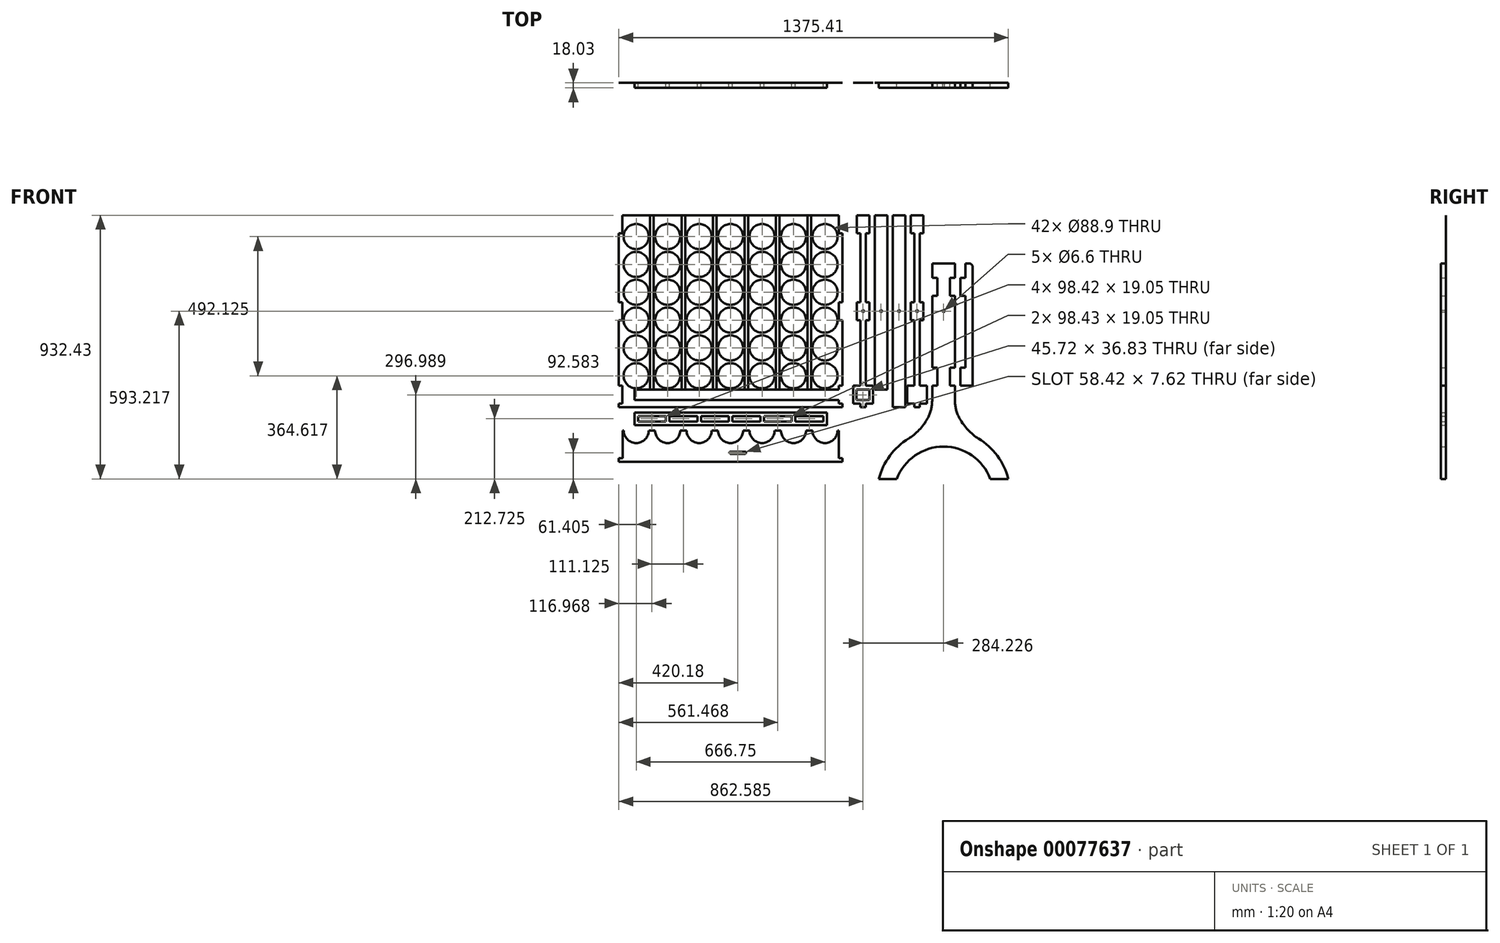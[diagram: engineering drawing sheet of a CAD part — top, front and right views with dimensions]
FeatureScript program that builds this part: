
annotation { "Feature Type Name" : "Feature", "Feature Type Description" : "" }
export const myFeature = defineFeature(function(context is Context, id is Id, definition is map)
    precondition{}
    {
        {
            assignVariable(context, id + "F0", {"name" : "Thickness", "anyValue" : .48});
        }
        {
            var Q0;
            Q0=qCreatedBy(makeId("Front.planeOp"),FACE);
            var sketch = newSketch(context, id + "F1", { "sketchPlane" : qUnion([Q0])});
            skLineSegment(sketch, "E0.bottom", {"start": v(-1056.26, 310.13) * mm, "end": v(-266.7, 310.13) * mm});
            skLineSegment(sketch, "E0.top", {"start": v(-1056.26, -368.3) * mm, "end": v(-266.7, -368.3) * mm});
            skLineSegment(sketch, "E0.left", {"start": v(-1056.26, 310.13) * mm, "end": v(-1056.26, -368.3) * mm});
            skLineSegment(sketch, "E0.right", {"start": v(-266.7, 310.13) * mm, "end": v(-266.7, -368.3) * mm});
            skCircle(sketch, "E1", {"center": v(-994.85, 234.44) * mm, "radius": 44.45 * mm});
            skLineSegment(sketch, "E2.bottom", {"start": v(-1056.26, 310.13) * mm, "end": v(-1044.07, 310.13) * mm});
            skLineSegment(sketch, "E2.right", {"start": v(-1044.07, 310.13) * mm, "end": v(-1044.07, -368.3) * mm, "construction": true});
            skLineSegment(sketch, "E3.0", {"start": v(-278.9, 310.13) * mm, "end": v(-278.9, -368.3) * mm, "construction": true});
            skLineSegment(sketch, "E4.top", {"start": v(-1056.26, 246.63) * mm, "end": v(-1044.07, 246.63) * mm});
            skLineSegment(sketch, "E4.left", {"start": v(-1056.26, 310.13) * mm, "end": v(-1056.26, 246.63) * mm});
            skLineSegment(sketch, "E4.right", {"start": v(-1044.07, 310.13) * mm, "end": v(-1044.07, 246.63) * mm});
            skLineSegment(sketch, "E5.bottom", {"start": v(-266.7, 310.13) * mm, "end": v(-278.9, 310.13) * mm});
            skLineSegment(sketch, "E5.top", {"start": v(-266.7, 246.63) * mm, "end": v(-278.9, 246.63) * mm});
            skLineSegment(sketch, "E5.left", {"start": v(-266.7, 310.13) * mm, "end": v(-266.7, 246.63) * mm});
            skLineSegment(sketch, "E5.right", {"start": v(-278.9, 310.13) * mm, "end": v(-278.9, 246.63) * mm});
            skLineSegment(sketch, "E6.top", {"start": v(-266.7, -292.1) * mm, "end": v(-278.9, -292.1) * mm});
            skLineSegment(sketch, "E6.left", {"start": v(-266.7, -368.3) * mm, "end": v(-266.7, -292.1) * mm});
            skLineSegment(sketch, "E6.right", {"start": v(-278.9, -355.6) * mm, "end": v(-278.9, -292.1) * mm});
            skLineSegment(sketch, "E7.bottom", {"start": v(-1056.26, 2.67) * mm, "end": v(-1044.07, 2.67) * mm});
            skLineSegment(sketch, "E7.top", {"start": v(-1056.26, -60.83) * mm, "end": v(-1044.07, -60.83) * mm});
            skLineSegment(sketch, "E7.left", {"start": v(-1056.26, 2.67) * mm, "end": v(-1056.26, -60.83) * mm});
            skLineSegment(sketch, "E7.right", {"start": v(-1044.07, 2.67) * mm, "end": v(-1044.07, -60.83) * mm});
            skPoint(sketch, "E8", {"position": v(-1056.26, -29.08) * mm});
            skLineSegment(sketch, "E9.MirrorCS", {"start": v(-266.7, -60.83) * mm, "end": v(-278.9, -60.83) * mm});
            skLineSegment(sketch, "E10.MirrorCS", {"start": v(-266.7, 2.67) * mm, "end": v(-278.9, 2.67) * mm});
            skLineSegment(sketch, "E11.MirrorCS", {"start": v(-266.7, 2.67) * mm, "end": v(-266.7, -60.83) * mm});
            skLineSegment(sketch, "E12.MirrorCS", {"start": v(-278.9, 2.67) * mm, "end": v(-278.9, -60.83) * mm});
            skLineSegment(sketch, "E13", {"start": v(-1044.07, -306.9) * mm, "end": v(-278.9, -306.9) * mm});
            skLineSegment(sketch, "E14", {"start": v(-945.64, 310.13) * mm, "end": v(-945.64, -306.9) * mm});
            skLineSegment(sketch, "E15", {"start": v(-932.94, 310.13) * mm, "end": v(-932.94, -306.9) * mm});
            skLineSegment(sketch, "E16.1.0.0", {"start": v(-821.82, 310.13) * mm, "end": v(-821.82, -306.9) * mm});
            skLineSegment(sketch, "E16.1.0.1", {"start": v(-834.52, 310.13) * mm, "end": v(-834.52, -306.9) * mm});
            skLineSegment(sketch, "E16.2.0.0", {"start": v(-710.7, 310.13) * mm, "end": v(-710.7, -306.9) * mm});
            skLineSegment(sketch, "E16.2.0.1", {"start": v(-723.4, 310.13) * mm, "end": v(-723.4, -306.9) * mm});
            skLineSegment(sketch, "E16.3.0.0", {"start": v(-599.57, 310.13) * mm, "end": v(-599.57, -306.9) * mm});
            skLineSegment(sketch, "E16.3.0.1", {"start": v(-612.27, 310.13) * mm, "end": v(-612.27, -306.9) * mm});
            skLineSegment(sketch, "E16.4.0.0", {"start": v(-488.44, 310.13) * mm, "end": v(-488.44, -306.9) * mm});
            skLineSegment(sketch, "E16.4.0.1", {"start": v(-501.14, 310.13) * mm, "end": v(-501.14, -306.9) * mm});
            skLineSegment(sketch, "E16.5.0.0", {"start": v(-377.32, 310.13) * mm, "end": v(-377.32, -306.9) * mm});
            skLineSegment(sketch, "E16.5.0.1", {"start": v(-390.02, 310.13) * mm, "end": v(-390.02, -306.9) * mm});
            skLineSegment(sketch, "E16.direction1", {"start": v(-932.94, -306.9) * mm, "end": v(-821.82, -306.9) * mm, "construction": true});
            skLineSegment(sketch, "E17.bottom", {"start": v(-994.85, -387.35) * mm, "end": v(-328.1, -387.35) * mm});
            skLineSegment(sketch, "E17.top", {"start": v(-994.85, -431.8) * mm, "end": v(-328.1, -431.8) * mm});
            skLineSegment(sketch, "E17.left", {"start": v(-994.85, -387.35) * mm, "end": v(-994.85, -431.8) * mm, "construction": true});
            skLineSegment(sketch, "E17.right", {"start": v(-328.1, -387.35) * mm, "end": v(-328.1, -431.8) * mm, "construction": true});
            skLineSegment(sketch, "E18.bottom", {"start": v(-988.5, -387.35) * mm, "end": v(-1001.2, -387.35) * mm});
            skLineSegment(sketch, "E18.top", {"start": v(-988.5, -431.8) * mm, "end": v(-1001.2, -431.8) * mm});
            skLineSegment(sketch, "E18.left", {"start": v(-988.5, -387.35) * mm, "end": v(-988.5, -431.8) * mm});
            skLineSegment(sketch, "E18.right", {"start": v(-1001.2, -387.35) * mm, "end": v(-1001.2, -431.8) * mm});
            skPoint(sketch, "E18.middle", {"position": v(-994.85, -409.58) * mm});
            skLineSegment(sketch, "E19.1.0.0", {"start": v(-877.38, -387.35) * mm, "end": v(-877.38, -431.8) * mm});
            skLineSegment(sketch, "E19.1.0.1", {"start": v(-890.08, -387.35) * mm, "end": v(-890.08, -431.8) * mm});
            skLineSegment(sketch, "E19.2.0.0", {"start": v(-766.25, -387.35) * mm, "end": v(-766.25, -431.8) * mm});
            skLineSegment(sketch, "E19.2.0.1", {"start": v(-778.95, -387.35) * mm, "end": v(-778.95, -431.8) * mm});
            skLineSegment(sketch, "E19.3.0.0", {"start": v(-655.13, -387.35) * mm, "end": v(-655.13, -431.8) * mm});
            skLineSegment(sketch, "E19.3.0.1", {"start": v(-667.83, -387.35) * mm, "end": v(-667.83, -431.8) * mm});
            skLineSegment(sketch, "E19.4.0.0", {"start": v(-544, -387.35) * mm, "end": v(-544, -431.8) * mm});
            skLineSegment(sketch, "E19.4.0.1", {"start": v(-556.7, -387.35) * mm, "end": v(-556.7, -431.8) * mm});
            skLineSegment(sketch, "E19.5.0.0", {"start": v(-432.88, -387.35) * mm, "end": v(-432.88, -431.8) * mm});
            skLineSegment(sketch, "E19.5.0.1", {"start": v(-445.58, -387.35) * mm, "end": v(-445.58, -431.8) * mm});
            skLineSegment(sketch, "E19.6.0.0", {"start": v(-321.75, -387.35) * mm, "end": v(-321.75, -431.8) * mm});
            skLineSegment(sketch, "E19.6.0.1", {"start": v(-334.45, -387.35) * mm, "end": v(-334.45, -431.8) * mm});
            skLineSegment(sketch, "E19.direction1", {"start": v(-988.5, -431.8) * mm, "end": v(-877.38, -431.8) * mm, "construction": true});
            skLineSegment(sketch, "E20", {"start": v(-321.75, -387.35) * mm, "end": v(-328.1, -387.35) * mm});
            skLineSegment(sketch, "E21", {"start": v(-321.75, -431.8) * mm, "end": v(-328.1, -431.8) * mm});
            skLineSegment(sketch, "E22", {"start": v(-988.5, -409.58) * mm, "end": v(-890.08, -409.58) * mm, "construction": true});
            skLineSegment(sketch, "E23.0", {"start": v(-988.5, -419.1) * mm, "end": v(-890.08, -419.1) * mm});
            skLineSegment(sketch, "E24.0", {"start": v(-988.5, -400.05) * mm, "end": v(-890.08, -400.05) * mm});
            skLineSegment(sketch, "E25.1.0.0", {"start": v(-877.38, -400.05) * mm, "end": v(-778.95, -400.05) * mm});
            skLineSegment(sketch, "E25.1.0.1", {"start": v(-877.38, -419.1) * mm, "end": v(-778.95, -419.1) * mm});
            skLineSegment(sketch, "E25.2.0.0", {"start": v(-766.25, -400.05) * mm, "end": v(-667.83, -400.05) * mm});
            skLineSegment(sketch, "E25.2.0.1", {"start": v(-766.25, -419.1) * mm, "end": v(-667.83, -419.1) * mm});
            skLineSegment(sketch, "E25.3.0.0", {"start": v(-655.13, -400.05) * mm, "end": v(-556.7, -400.05) * mm});
            skLineSegment(sketch, "E25.3.0.1", {"start": v(-655.13, -419.1) * mm, "end": v(-556.7, -419.1) * mm});
            skLineSegment(sketch, "E25.4.0.0", {"start": v(-544, -400.05) * mm, "end": v(-445.58, -400.05) * mm});
            skLineSegment(sketch, "E25.4.0.1", {"start": v(-544, -419.1) * mm, "end": v(-445.58, -419.1) * mm});
            skLineSegment(sketch, "E25.5.0.0", {"start": v(-432.88, -400.05) * mm, "end": v(-334.45, -400.05) * mm});
            skLineSegment(sketch, "E25.5.0.1", {"start": v(-432.88, -419.1) * mm, "end": v(-334.45, -419.1) * mm});
            skLineSegment(sketch, "E25.direction1", {"start": v(-988.5, -400.05) * mm, "end": v(-877.38, -400.05) * mm, "construction": true});
            skLineSegment(sketch, "E26.0", {"start": v(-1044.07, -343.73) * mm, "end": v(-278.9, -343.73) * mm});
            skLineSegment(sketch, "E27", {"start": v(-278.9, -355.6) * mm, "end": v(-266.7, -355.6) * mm});
            skLineSegment(sketch, "E28", {"start": v(-661.48, -368.3) * mm, "end": v(-661.48, -343.73) * mm, "construction": true});
            skLineSegment(sketch, "E29.MirrorCS", {"start": v(-1044.07, -355.6) * mm, "end": v(-1056.26, -355.6) * mm});
            skLineSegment(sketch, "E30.MirrorCS", {"start": v(-1044.07, -355.6) * mm, "end": v(-1044.07, -292.1) * mm});
            skLineSegment(sketch, "E31.MirrorCS", {"start": v(-1056.26, -292.1) * mm, "end": v(-1044.07, -292.1) * mm});
            skLineSegment(sketch, "E32", {"start": v(-1001.2, -343.73) * mm, "end": v(-1001.2, -306.9) * mm});
            skLineSegment(sketch, "E33.bottom", {"start": v(-215.9, 310.13) * mm, "end": v(-171.45, 310.13) * mm, "construction": true});
            skLineSegment(sketch, "E34.bottom", {"start": v(-228.1, -355.6) * mm, "end": v(-203.7, -355.6) * mm});
            skLineSegment(sketch, "E34.top", {"start": v(-228.1, -292.1) * mm, "end": v(-203.7, -292.1) * mm});
            skLineSegment(sketch, "E34.left", {"start": v(-228.1, -355.6) * mm, "end": v(-228.1, -292.1) * mm});
            skLineSegment(sketch, "E34.right", {"start": v(-203.7, -355.6) * mm, "end": v(-203.7, -292.1) * mm});
            skLineSegment(sketch, "E35", {"start": v(-193.67, -368.3) * mm, "end": v(-193.67, 310.13) * mm, "construction": true});
            skLineSegment(sketch, "E36.bottom", {"start": v(-215.9, 2.67) * mm, "end": v(-203.7, 2.67) * mm});
            skLineSegment(sketch, "E36.top", {"start": v(-215.9, -60.83) * mm, "end": v(-203.7, -60.83) * mm});
            skLineSegment(sketch, "E36.left", {"start": v(-215.9, 2.67) * mm, "end": v(-215.9, -60.83) * mm});
            skLineSegment(sketch, "E36.right", {"start": v(-203.7, 2.67) * mm, "end": v(-203.7, -60.83) * mm});
            skLineSegment(sketch, "E37.bottom", {"start": v(-215.9, 310.13) * mm, "end": v(-203.7, 310.13) * mm});
            skLineSegment(sketch, "E37.top", {"start": v(-215.9, 246.63) * mm, "end": v(-203.7, 246.63) * mm});
            skLineSegment(sketch, "E37.left", {"start": v(-215.9, 310.13) * mm, "end": v(-215.9, 246.63) * mm});
            skLineSegment(sketch, "E37.right", {"start": v(-203.7, 310.13) * mm, "end": v(-203.7, 246.63) * mm});
            skLineSegment(sketch, "E38.MirrorCS", {"start": v(-171.45, 310.13) * mm, "end": v(-171.45, 246.63) * mm});
            skLineSegment(sketch, "E39.MirrorCS", {"start": v(-171.45, 310.13) * mm, "end": v(-183.64, 310.13) * mm});
            skLineSegment(sketch, "E40.MirrorCS", {"start": v(-183.64, 310.13) * mm, "end": v(-183.64, 246.63) * mm});
            skLineSegment(sketch, "E41.MirrorCS", {"start": v(-171.45, 246.63) * mm, "end": v(-183.64, 246.63) * mm});
            skLineSegment(sketch, "E42.MirrorCS", {"start": v(-171.45, 2.67) * mm, "end": v(-171.45, -60.83) * mm});
            skLineSegment(sketch, "E43.MirrorCS", {"start": v(-171.45, -60.83) * mm, "end": v(-183.64, -60.83) * mm});
            skLineSegment(sketch, "E44.MirrorCS", {"start": v(-183.64, 2.67) * mm, "end": v(-183.64, -60.83) * mm});
            skLineSegment(sketch, "E45.MirrorCS", {"start": v(-171.45, 2.67) * mm, "end": v(-183.64, 2.67) * mm});
            skLineSegment(sketch, "E46.MirrorCS", {"start": v(-159.26, -355.6) * mm, "end": v(-159.26, -292.1) * mm});
            skLineSegment(sketch, "E47.MirrorCS", {"start": v(-159.26, -355.6) * mm, "end": v(-183.64, -355.6) * mm});
            skLineSegment(sketch, "E48.MirrorCS", {"start": v(-159.26, -292.1) * mm, "end": v(-183.64, -292.1) * mm});
            skLineSegment(sketch, "E49.MirrorCS", {"start": v(-183.64, -355.6) * mm, "end": v(-183.64, -292.1) * mm});
            skLineSegment(sketch, "E50.bottom", {"start": v(-203.7, -368.3) * mm, "end": v(-183.64, -368.3) * mm});
            skLineSegment(sketch, "E50.top", {"start": v(-203.7, 310.13) * mm, "end": v(-183.64, 310.13) * mm});
            skLineSegment(sketch, "E50.left", {"start": v(-203.7, -368.3) * mm, "end": v(-203.7, 310.13) * mm});
            skLineSegment(sketch, "E50.right", {"start": v(-183.64, -368.3) * mm, "end": v(-183.64, 310.13) * mm});
            skLineSegment(sketch, "E51.bottom", {"start": v(-216.54, -306.9) * mm, "end": v(-170.82, -306.9) * mm});
            skLineSegment(sketch, "E51.top", {"start": v(-216.54, -343.73) * mm, "end": v(-170.82, -343.73) * mm});
            skLineSegment(sketch, "E51.left", {"start": v(-216.54, -306.9) * mm, "end": v(-216.54, -343.73) * mm});
            skLineSegment(sketch, "E51.right", {"start": v(-170.82, -306.9) * mm, "end": v(-170.82, -343.73) * mm});
            skPoint(sketch, "E52", {"position": v(-193.68, -306.9) * mm});
            skLineSegment(sketch, "E53.bottom", {"start": v(-152.4, 310.13) * mm, "end": v(-107.95, 310.13) * mm});
            skLineSegment(sketch, "E53.top", {"start": v(-152.4, -368.3) * mm, "end": v(-107.95, -368.3) * mm, "construction": true});
            skLineSegment(sketch, "E53.left", {"start": v(-152.4, 310.13) * mm, "end": v(-152.4, -368.3) * mm});
            skLineSegment(sketch, "E53.right", {"start": v(-107.95, 310.13) * mm, "end": v(-107.95, -368.3) * mm});
            skLineSegment(sketch, "E54.0", {"start": v(-98.43, 532.38) * mm, "end": v(-98.43, -368.3) * mm, "construction": true});
            skLineSegment(sketch, "E55.MirrorCS", {"start": v(19.05, 310.13) * mm, "end": v(6.86, 310.13) * mm});
            skLineSegment(sketch, "E56.MirrorCS", {"start": v(-25.4, 310.13) * mm, "end": v(-13.2, 310.13) * mm});
            skLineSegment(sketch, "E57.MirrorCS", {"start": v(-37.6, -355.6) * mm, "end": v(-13.2, -355.6) * mm});
            skLineSegment(sketch, "E58.MirrorCS", {"start": v(31.24, -355.6) * mm, "end": v(6.86, -355.6) * mm});
            skLineSegment(sketch, "E59.MirrorCS", {"start": v(19.05, -60.83) * mm, "end": v(6.86, -60.83) * mm});
            skLineSegment(sketch, "E60.MirrorCS", {"start": v(19.05, 246.63) * mm, "end": v(6.86, 246.63) * mm});
            skLineSegment(sketch, "E61.MirrorCS", {"start": v(19.05, 310.13) * mm, "end": v(-25.4, 310.13) * mm, "construction": true});
            skLineSegment(sketch, "E62.MirrorCS", {"start": v(-37.6, -292.1) * mm, "end": v(-13.2, -292.1) * mm});
            skLineSegment(sketch, "E63.MirrorCS", {"start": v(-25.4, 246.63) * mm, "end": v(-13.2, 246.63) * mm});
            skLineSegment(sketch, "E64.MirrorCS", {"start": v(31.24, -292.1) * mm, "end": v(6.86, -292.1) * mm});
            skLineSegment(sketch, "E65.MirrorCS", {"start": v(-25.4, -60.83) * mm, "end": v(-13.2, -60.83) * mm});
            skLineSegment(sketch, "E66.MirrorCS", {"start": v(19.05, 2.67) * mm, "end": v(6.86, 2.67) * mm});
            skLineSegment(sketch, "E67.MirrorCS", {"start": v(-25.4, 2.67) * mm, "end": v(-13.2, 2.67) * mm});
            skLineSegment(sketch, "E68.MirrorCS", {"start": v(6.86, 310.13) * mm, "end": v(-13.2, 310.13) * mm});
            skLineSegment(sketch, "E69.MirrorCS", {"start": v(6.86, 2.67) * mm, "end": v(6.86, -60.83) * mm});
            skLineSegment(sketch, "E70.MirrorCS", {"start": v(-13.2, -355.6) * mm, "end": v(-13.2, -292.1) * mm});
            skLineSegment(sketch, "E71.MirrorCS", {"start": v(6.86, -368.3) * mm, "end": v(-13.2, -368.3) * mm});
            skLineSegment(sketch, "E72.MirrorCS", {"start": v(-44.45, -368.3) * mm, "end": v(-88.9, -368.3) * mm});
            skLineSegment(sketch, "E73.MirrorCS", {"start": v(-25.4, 2.67) * mm, "end": v(-25.4, -60.83) * mm});
            skLineSegment(sketch, "E74.MirrorCS", {"start": v(-13.2, 2.67) * mm, "end": v(-13.2, -60.83) * mm});
            skLineSegment(sketch, "E75.MirrorCS", {"start": v(6.86, -355.6) * mm, "end": v(6.86, -292.1) * mm});
            skLineSegment(sketch, "E76.MirrorCS", {"start": v(-37.6, -355.6) * mm, "end": v(-37.6, -292.1) * mm});
            skLineSegment(sketch, "E77.MirrorCS", {"start": v(19.05, 2.67) * mm, "end": v(19.05, -60.83) * mm});
            skLineSegment(sketch, "E78.MirrorCS", {"start": v(-13.2, -368.3) * mm, "end": v(-13.2, 310.13) * mm});
            skLineSegment(sketch, "E79.MirrorCS", {"start": v(-13.2, 310.13) * mm, "end": v(-13.2, 246.63) * mm});
            skPoint(sketch, "E80.MirrorP", {"position": v(-3.18, -306.9) * mm});
            skLineSegment(sketch, "E81.MirrorCS", {"start": v(-25.4, 310.13) * mm, "end": v(-25.4, 246.63) * mm});
            skLineSegment(sketch, "E82.MirrorCS", {"start": v(6.86, 310.13) * mm, "end": v(6.86, 246.63) * mm});
            skLineSegment(sketch, "E83.MirrorCS", {"start": v(19.05, 310.13) * mm, "end": v(19.05, 246.63) * mm});
            skLineSegment(sketch, "E84.MirrorCS", {"start": v(6.86, -368.3) * mm, "end": v(6.86, 310.13) * mm});
            skLineSegment(sketch, "E85.MirrorCS", {"start": v(31.24, -355.6) * mm, "end": v(31.24, -292.1) * mm});
            skLineSegment(sketch, "E86.MirrorCS", {"start": v(-44.45, 310.13) * mm, "end": v(-88.9, 310.13) * mm});
            skLineSegment(sketch, "E87.MirrorCS", {"start": v(-44.45, 310.13) * mm, "end": v(-44.45, -368.3) * mm});
            skLineSegment(sketch, "E88.MirrorCS", {"start": v(-88.9, 310.13) * mm, "end": v(-88.9, -368.3) * mm});
            skLineSegment(sketch, "E89.MirrorCS", {"start": v(-3.18, -368.3) * mm, "end": v(-3.18, 310.13) * mm, "construction": true});
            skLineSegment(sketch, "E90.bottom", {"start": v(-152.4, -306.9) * mm, "end": v(-107.95, -306.9) * mm});
            skLineSegment(sketch, "E90.top", {"start": v(-152.4, -343.73) * mm, "end": v(-107.95, -343.73) * mm, "construction": true});
            skLineSegment(sketch, "E90.left", {"start": v(-152.4, -306.9) * mm, "end": v(-152.4, -343.73) * mm});
            skLineSegment(sketch, "E90.right", {"start": v(-107.95, -306.9) * mm, "end": v(-107.95, -343.73) * mm});
            skLineSegment(sketch, "E91.bottom", {"start": v(-1056.26, -450.85) * mm, "end": v(-266.7, -450.85) * mm});
            skLineSegment(sketch, "E91.top", {"start": v(-1056.26, -561.47) * mm, "end": v(-266.7, -561.47) * mm});
            skLineSegment(sketch, "E91.left", {"start": v(-1056.26, -450.85) * mm, "end": v(-1056.26, -561.47) * mm});
            skLineSegment(sketch, "E91.right", {"start": v(-266.7, -450.85) * mm, "end": v(-266.7, -561.47) * mm});
            skLineSegment(sketch, "E92.bottom", {"start": v(50.3, -368.3) * mm, "end": v(130.8, -368.3) * mm, "construction": true});
            skLineSegment(sketch, "E92.top", {"start": v(50.3, 139.7) * mm, "end": v(130.8, 139.7) * mm});
            skLineSegment(sketch, "E92.left", {"start": v(50.3, -368.3) * mm, "end": v(50.3, 139.7) * mm});
            skLineSegment(sketch, "E92.right", {"start": v(130.8, -368.3) * mm, "end": v(130.8, 139.7) * mm});
            skLineSegment(sketch, "E93", {"start": v(50.3, -368.3) * mm, "end": v(-31.4, -478.48) * mm});
            skLineSegment(sketch, "E94", {"start": v(-138.05, -622.3) * mm, "end": v(319.15, -622.3) * mm});
            skLineSegment(sketch, "E95", {"start": v(319.15, -622.3) * mm, "end": v(212.5, -478.48) * mm, "construction": true});
            skLineSegment(sketch, "E96", {"start": v(90.55, -368.3) * mm, "end": v(90.55, -622.3) * mm, "construction": true});
            skLineSegment(sketch, "E97.bottom", {"start": v(50.3, -292.1) * mm, "end": v(68.33, -292.1) * mm});
            skLineSegment(sketch, "E97.top", {"start": v(50.3, -228.6) * mm, "end": v(68.33, -228.6) * mm});
            skLineSegment(sketch, "E97.left", {"start": v(50.3, -292.1) * mm, "end": v(50.3, -228.6) * mm});
            skLineSegment(sketch, "E97.right", {"start": v(68.33, -292.1) * mm, "end": v(68.33, -228.6) * mm});
            skLineSegment(sketch, "E98.bottom", {"start": v(50.3, 88.9) * mm, "end": v(68.33, 88.9) * mm});
            skLineSegment(sketch, "E98.top", {"start": v(50.3, 25.4) * mm, "end": v(68.33, 25.4) * mm});
            skLineSegment(sketch, "E98.left", {"start": v(50.3, 88.9) * mm, "end": v(50.3, 25.4) * mm});
            skLineSegment(sketch, "E98.right", {"start": v(68.33, 88.9) * mm, "end": v(68.33, 25.4) * mm});
            skLineSegment(sketch, "E99.MirrorCS", {"start": v(130.8, -292.1) * mm, "end": v(112.78, -292.1) * mm});
            skLineSegment(sketch, "E100.MirrorCS", {"start": v(130.81, -228.6) * mm, "end": v(112.78, -228.6) * mm});
            skLineSegment(sketch, "E101.MirrorCS", {"start": v(130.81, -292.1) * mm, "end": v(130.81, -228.6) * mm});
            skLineSegment(sketch, "E102.MirrorCS", {"start": v(112.78, -292.1) * mm, "end": v(112.78, -228.6) * mm});
            skLineSegment(sketch, "E103.MirrorCS", {"start": v(130.81, 88.9) * mm, "end": v(130.81, 25.4) * mm});
            skLineSegment(sketch, "E104.MirrorCS", {"start": v(130.81, 25.4) * mm, "end": v(112.78, 25.4) * mm});
            skLineSegment(sketch, "E105.MirrorCS", {"start": v(112.78, 88.9) * mm, "end": v(112.78, 25.4) * mm});
            skLineSegment(sketch, "E106.MirrorCS", {"start": v(130.81, 88.9) * mm, "end": v(112.78, 88.9) * mm});
            skLineSegment(sketch, "E107.bottom", {"start": v(167.9, 139.7) * mm, "end": v(193.3, 139.7) * mm});
            skLineSegment(sketch, "E107.top", {"start": v(167.9, -292.1) * mm, "end": v(193.3, -292.1) * mm});
            skLineSegment(sketch, "E107.left", {"start": v(167.9, 139.7) * mm, "end": v(167.9, -292.1) * mm});
            skLineSegment(sketch, "E107.right", {"start": v(193.3, 139.7) * mm, "end": v(193.3, -292.1) * mm});
            skLineSegment(sketch, "E108.bottom", {"start": v(167.9, -292.1) * mm, "end": v(149.86, -292.1) * mm});
            skLineSegment(sketch, "E108.top", {"start": v(167.9, -228.6) * mm, "end": v(149.86, -228.6) * mm});
            skLineSegment(sketch, "E108.left", {"start": v(167.9, -292.1) * mm, "end": v(167.9, -228.6) * mm});
            skLineSegment(sketch, "E108.right", {"start": v(149.86, -292.1) * mm, "end": v(149.86, -228.6) * mm});
            skLineSegment(sketch, "E109.bottom", {"start": v(167.9, 88.9) * mm, "end": v(149.86, 88.9) * mm});
            skLineSegment(sketch, "E109.top", {"start": v(167.9, 25.4) * mm, "end": v(149.86, 25.4) * mm});
            skLineSegment(sketch, "E109.left", {"start": v(167.9, 88.9) * mm, "end": v(167.9, 25.4) * mm});
            skLineSegment(sketch, "E109.right", {"start": v(149.86, 88.9) * mm, "end": v(149.86, 25.4) * mm});
            skCircle(sketch, "E110", {"center": v(-3.18, -29.08) * mm, "radius": 3.3 * mm});
            skLineSegment(sketch, "E111", {"start": v(90.55, 139.7) * mm, "end": v(90.55, -29.08) * mm, "construction": true});
            skCircle(sketch, "E112", {"center": v(90.55, -29.08) * mm, "radius": 3.3 * mm});
            skCircle(sketch, "E113.MirrorC", {"center": v(-193.67, -29.08) * mm, "radius": 3.3 * mm});
            skCircle(sketch, "E114", {"center": v(-66.68, -29.08) * mm, "radius": 3.3 * mm});
            skPoint(sketch, "E114.centerSnap0", {"position": v(-25.4, -29.08) * mm});
            skPoint(sketch, "E114.centerSnap1", {"position": v(-66.68, 310.13) * mm});
            skCircle(sketch, "E115.MirrorC", {"center": v(-130.18, -29.08) * mm, "radius": 3.3 * mm});
            skLineSegment(sketch, "E116.top", {"start": v(-74.55, -609.6) * mm, "end": v(255.65, -609.6) * mm, "construction": true});
            skLineSegment(sketch, "E116.left", {"start": v(-74.55, -622.3) * mm, "end": v(-74.55, -609.6) * mm});
            skLineSegment(sketch, "E116.right", {"start": v(255.65, -622.3) * mm, "end": v(255.65, -609.6) * mm});
            skPoint(sketch, "E117", {"position": v(90.55, -609.6) * mm});
            skPoint(sketch, "E118", {"position": v(-130.18, -343.73) * mm});
            skLineSegment(sketch, "E119", {"start": v(-130.18, -368.3) * mm, "end": v(-130.18, -292.1) * mm, "construction": true});
            skArc(sketch, "E120", {"start": v(319.15, -622.3) * mm, "mid": v(90.55, -444.5) * mm, "end": v(-138.05, -622.3) * mm});
            skLineSegment(sketch, "E121", {"start": v(-31.4, -478.48) * mm, "end": v(-138.05, -622.3) * mm, "construction": true});
            skLineSegment(sketch, "E122", {"start": v(212.5, -478.48) * mm, "end": v(130.81, -368.3) * mm});
            skArc(sketch, "E123", {"start": v(-31.4, -478.48) * mm, "mid": v(19.65, -430.95) * mm, "end": v(50.3, -368.3) * mm});
            skArc(sketch, "E124", {"start": v(255.65, -622.3) * mm, "mid": v(90.55, -508) * mm, "end": v(-74.55, -622.3) * mm});
            skArc(sketch, "E125.MirrorCS", {"start": v(212.5, -478.48) * mm, "mid": v(161.46, -430.95) * mm, "end": v(130.81, -368.3) * mm});
            skArc(sketch, "E126.MirrorC", {"start": v(-394.78, -450.85) * mm, "mid": v(-439.23, -495.3) * mm, "end": v(-483.68, -450.85) * mm});
            skArc(sketch, "E127.MirrorC", {"start": v(-283.65, -450.85) * mm, "mid": v(-328.1, -495.3) * mm, "end": v(-372.55, -450.85) * mm});
            skArc(sketch, "E128.trimOffspring", {"start": v(-950.4, -450.85) * mm, "mid": v(-994.85, -495.3) * mm, "end": v(-1039.3, -450.85) * mm});
            skArc(sketch, "E129.trimOffspring", {"start": v(-839.28, -450.85) * mm, "mid": v(-883.73, -495.3) * mm, "end": v(-928.18, -450.85) * mm});
            skArc(sketch, "E130.trimOffspring", {"start": v(-728.15, -450.85) * mm, "mid": v(-772.6, -495.3) * mm, "end": v(-817.05, -450.85) * mm});
            skArc(sketch, "E131.trimOffspring", {"start": v(-617.03, -450.85) * mm, "mid": v(-661.48, -495.3) * mm, "end": v(-705.93, -450.85) * mm});
            skArc(sketch, "E132.trimOffspring", {"start": v(-505.9, -450.85) * mm, "mid": v(-550.35, -495.3) * mm, "end": v(-594.8, -450.85) * mm});
            skLineSegment(sketch, "E133.bottom", {"start": v(-1056.26, -485.27) * mm, "end": v(-1043.05, -485.27) * mm});
            skLineSegment(sketch, "E133.top", {"start": v(-1056.26, -450.85) * mm, "end": v(-1043.05, -450.85) * mm});
            skLineSegment(sketch, "E133.left", {"start": v(-1056.26, -485.27) * mm, "end": v(-1056.26, -450.85) * mm, "construction": true});
            skLineSegment(sketch, "E133.right", {"start": v(-1043.05, -485.27) * mm, "end": v(-1043.05, -450.85) * mm});
            skLineSegment(sketch, "E134.bottom", {"start": v(-1056.26, -450.85) * mm, "end": v(-1068.45, -450.85) * mm, "construction": true});
            skLineSegment(sketch, "E134.top", {"start": v(-1056.26, -485.27) * mm, "end": v(-1068.45, -485.27) * mm, "construction": true});
            skLineSegment(sketch, "E134.left", {"start": v(-1056.26, -450.85) * mm, "end": v(-1056.26, -485.27) * mm, "construction": true});
            skLineSegment(sketch, "E134.right", {"start": v(-1068.45, -450.85) * mm, "end": v(-1068.45, -485.27) * mm, "construction": true});
            skLineSegment(sketch, "E135.MirrorCS", {"start": v(-279.9, -485.27) * mm, "end": v(-279.9, -450.85) * mm});
            skLineSegment(sketch, "E136", {"start": v(-279.9, -485.27) * mm, "end": v(-266.7, -485.27) * mm});
            skLineSegment(sketch, "E137.top", {"start": v(-279.9, -548.77) * mm, "end": v(-266.7, -548.77) * mm});
            skLineSegment(sketch, "E137.left", {"start": v(-279.9, -485.27) * mm, "end": v(-279.9, -548.77) * mm});
            skLineSegment(sketch, "E137.right", {"start": v(-266.7, -485.27) * mm, "end": v(-266.7, -548.77) * mm});
            skLineSegment(sketch, "E138.MirrorCS", {"start": v(-1043.05, -485.27) * mm, "end": v(-1043.05, -548.77) * mm});
            skLineSegment(sketch, "E139.MirrorCS", {"start": v(-1043.05, -548.77) * mm, "end": v(-1056.26, -548.77) * mm});
            skLineSegment(sketch, "E140", {"start": v(-661.48, -529.72) * mm, "end": v(-610.68, -529.72) * mm});
            skArc(sketch, "E141.0.startCap", {"start": v(-661.48, -533.53) * mm, "mid": v(-665.29, -529.72) * mm, "end": v(-661.48, -525.9) * mm});
            skArc(sketch, "E141.0.endCap", {"start": v(-610.68, -525.9) * mm, "mid": v(-606.87, -529.72) * mm, "end": v(-610.68, -533.53) * mm});
            skLineSegment(sketch, "E141.0.left", {"start": v(-661.48, -525.9) * mm, "end": v(-610.68, -525.9) * mm});
            skLineSegment(sketch, "E141.0.right", {"start": v(-661.48, -533.53) * mm, "end": v(-610.68, -533.53) * mm});
            skCircle(sketch, "E142.0.1.0", {"center": v(-994.85, 136.02) * mm, "radius": 44.45 * mm});
            skCircle(sketch, "E142.0.2.0", {"center": v(-994.85, 37.6) * mm, "radius": 44.45 * mm});
            skCircle(sketch, "E142.0.3.0", {"center": v(-994.85, -60.83) * mm, "radius": 44.45 * mm});
            skCircle(sketch, "E142.0.4.0", {"center": v(-994.85, -159.26) * mm, "radius": 44.45 * mm});
            skCircle(sketch, "E142.0.5.0", {"center": v(-994.85, -257.68) * mm, "radius": 44.45 * mm});
            skCircle(sketch, "E142.1.0.0", {"center": v(-883.73, 234.44) * mm, "radius": 44.45 * mm});
            skCircle(sketch, "E142.1.1.0", {"center": v(-883.73, 136.02) * mm, "radius": 44.45 * mm});
            skCircle(sketch, "E142.1.2.0", {"center": v(-883.73, 37.6) * mm, "radius": 44.45 * mm});
            skCircle(sketch, "E142.1.3.0", {"center": v(-883.73, -60.83) * mm, "radius": 44.45 * mm});
            skCircle(sketch, "E142.1.4.0", {"center": v(-883.73, -159.26) * mm, "radius": 44.45 * mm});
            skCircle(sketch, "E142.1.5.0", {"center": v(-883.73, -257.68) * mm, "radius": 44.45 * mm});
            skCircle(sketch, "E142.2.0.0", {"center": v(-772.6, 234.44) * mm, "radius": 44.45 * mm});
            skCircle(sketch, "E142.2.1.0", {"center": v(-772.6, 136.02) * mm, "radius": 44.45 * mm});
            skCircle(sketch, "E142.2.2.0", {"center": v(-772.6, 37.6) * mm, "radius": 44.45 * mm});
            skCircle(sketch, "E142.2.3.0", {"center": v(-772.6, -60.83) * mm, "radius": 44.45 * mm});
            skCircle(sketch, "E142.2.4.0", {"center": v(-772.6, -159.26) * mm, "radius": 44.45 * mm});
            skCircle(sketch, "E142.2.5.0", {"center": v(-772.6, -257.68) * mm, "radius": 44.45 * mm});
            skCircle(sketch, "E142.3.0.0", {"center": v(-661.48, 234.44) * mm, "radius": 44.45 * mm});
            skCircle(sketch, "E142.3.1.0", {"center": v(-661.48, 136.02) * mm, "radius": 44.45 * mm});
            skCircle(sketch, "E142.3.2.0", {"center": v(-661.48, 37.6) * mm, "radius": 44.45 * mm});
            skCircle(sketch, "E142.3.3.0", {"center": v(-661.48, -60.83) * mm, "radius": 44.45 * mm});
            skCircle(sketch, "E142.3.4.0", {"center": v(-661.48, -159.26) * mm, "radius": 44.45 * mm});
            skCircle(sketch, "E142.3.5.0", {"center": v(-661.48, -257.68) * mm, "radius": 44.45 * mm});
            skCircle(sketch, "E142.4.0.0", {"center": v(-550.35, 234.44) * mm, "radius": 44.45 * mm});
            skCircle(sketch, "E142.4.1.0", {"center": v(-550.35, 136.02) * mm, "radius": 44.45 * mm});
            skCircle(sketch, "E142.4.2.0", {"center": v(-550.35, 37.6) * mm, "radius": 44.45 * mm});
            skCircle(sketch, "E142.4.3.0", {"center": v(-550.35, -60.83) * mm, "radius": 44.45 * mm});
            skCircle(sketch, "E142.4.4.0", {"center": v(-550.35, -159.26) * mm, "radius": 44.45 * mm});
            skCircle(sketch, "E142.4.5.0", {"center": v(-550.35, -257.68) * mm, "radius": 44.45 * mm});
            skCircle(sketch, "E142.5.0.0", {"center": v(-439.23, 234.44) * mm, "radius": 44.45 * mm});
            skCircle(sketch, "E142.5.1.0", {"center": v(-439.23, 136.02) * mm, "radius": 44.45 * mm});
            skCircle(sketch, "E142.5.2.0", {"center": v(-439.23, 37.6) * mm, "radius": 44.45 * mm});
            skCircle(sketch, "E142.5.3.0", {"center": v(-439.23, -60.83) * mm, "radius": 44.45 * mm});
            skCircle(sketch, "E142.5.4.0", {"center": v(-439.23, -159.26) * mm, "radius": 44.45 * mm});
            skCircle(sketch, "E142.5.5.0", {"center": v(-439.23, -257.68) * mm, "radius": 44.45 * mm});
            skCircle(sketch, "E142.6.0.0", {"center": v(-328.1, 234.44) * mm, "radius": 44.45 * mm});
            skCircle(sketch, "E142.6.1.0", {"center": v(-328.1, 136.02) * mm, "radius": 44.45 * mm});
            skCircle(sketch, "E142.6.2.0", {"center": v(-328.1, 37.6) * mm, "radius": 44.45 * mm});
            skCircle(sketch, "E142.6.3.0", {"center": v(-328.1, -60.83) * mm, "radius": 44.45 * mm});
            skCircle(sketch, "E142.6.4.0", {"center": v(-328.1, -159.26) * mm, "radius": 44.45 * mm});
            skCircle(sketch, "E142.6.5.0", {"center": v(-328.1, -257.68) * mm, "radius": 44.45 * mm});
            skLineSegment(sketch, "E142.direction1", {"start": v(-994.85, 234.44) * mm, "end": v(-883.73, 234.44) * mm, "construction": true});
            skLineSegment(sketch, "E142.direction2", {"start": v(-994.85, 234.44) * mm, "end": v(-994.85, 136.02) * mm, "construction": true});
            skCircle(sketch, "E143", {"center": v(-994.85, -257.68) * mm, "radius": 49.21 * mm, "construction": true});
            skSolve(sketch);
        }
        {
            var Q0;
            Q0=makeQuery(id+"F1.imprint","IMPRINT",FACE,{"disambiguationData":[TD([[makeQuery(id+"F1.imprint","IMPRINT",EDGE,{"derivedFrom":sQuery(id+"F1.wireOp",EDGE,"b72d2d66-4ce2-4289-90ab-e637a022988c.0.6.0")}),-1.0]])]});
            var Q1;
            Q1=makeQuery(id+"F1.imprint","IMPRINT",FACE,{"disambiguationData":[TD([[makeQuery(id+"F1.imprint","IMPRINT",EDGE,{"derivedFrom":sQuery(id+"F1.wireOp",EDGE,"E1")}),-1.0]])]});
            var Q2;
            Q2=makeQuery(id+"F1.imprint","IMPRINT",FACE,{"disambiguationData":[TD([[makeQuery(id+"F1.imprint","IMPRINT",EDGE,{"derivedFrom":sQuery(id+"F1.wireOp",EDGE,"e17ad13c-0773-4227-a656-80a7ee0610df.1.0.0")}),-1.0]])]});
            var Q3;
            Q3=makeQuery(id+"F1.imprint","IMPRINT",FACE,{"disambiguationData":[TD([[makeQuery(id+"F1.imprint","IMPRINT",EDGE,{"derivedFrom":sQuery(id+"F1.wireOp",EDGE,"e17ad13c-0773-4227-a656-80a7ee0610df.2.0.0")}),-1.0]])]});
            var Q4;
            Q4=makeQuery(id+"F1.imprint","IMPRINT",FACE,{"disambiguationData":[TD([[makeQuery(id+"F1.imprint","IMPRINT",EDGE,{"derivedFrom":sQuery(id+"F1.wireOp",EDGE,"e17ad13c-0773-4227-a656-80a7ee0610df.3.0.0")}),-1.0]])]});
            var Q5;
            Q5=makeQuery(id+"F1.imprint","IMPRINT",FACE,{"disambiguationData":[TD([[makeQuery(id+"F1.imprint","IMPRINT",EDGE,{"derivedFrom":sQuery(id+"F1.wireOp",EDGE,"e17ad13c-0773-4227-a656-80a7ee0610df.4.0.0")}),-1.0]])]});
            var Q6;
            Q6=makeQuery(id+"F1.imprint","IMPRINT",FACE,{"disambiguationData":[TD([[makeQuery(id+"F1.imprint","IMPRINT",EDGE,{"derivedFrom":sQuery(id+"F1.wireOp",EDGE,"e17ad13c-0773-4227-a656-80a7ee0610df.5.0.0")}),-1.0]])]});
            var Q7;
            Q7=makeQuery(id+"F1.imprint","IMPRINT",FACE,{"disambiguationData":[TD([[makeQuery(id+"F1.imprint","IMPRINT",EDGE,{"derivedFrom":sQuery(id+"F1.wireOp",EDGE,"XpdAvdAL-t41n-kh1d-zuyA-r62Oe6xQwDXB")}),-1.0]])]});
            var Q8;
            Q8=makeQuery(id+"F1.imprint","IMPRINT",FACE,{"disambiguationData":[TD([[makeQuery(id+"F1.imprint","IMPRINT",EDGE,{"derivedFrom":sQuery(id+"F1.wireOp",EDGE,"c9cc7f5d-6211-4dc9-b41b-aaae2feddd97.1.0.0")}),-1.0]])]});
            var Q9;
            Q9=makeQuery(id+"F1.imprint","IMPRINT",FACE,{"disambiguationData":[TD([[makeQuery(id+"F1.imprint","IMPRINT",EDGE,{"derivedFrom":sQuery(id+"F1.wireOp",EDGE,"c9cc7f5d-6211-4dc9-b41b-aaae2feddd97.2.0.0")}),-1.0]])]});
            var Q10;
            Q10=makeQuery(id+"F1.imprint","IMPRINT",FACE,{"disambiguationData":[TD([[makeQuery(id+"F1.imprint","IMPRINT",EDGE,{"derivedFrom":sQuery(id+"F1.wireOp",EDGE,"c9cc7f5d-6211-4dc9-b41b-aaae2feddd97.3.0.0")}),-1.0]])]});
            var Q11;
            Q11=makeQuery(id+"F1.imprint","IMPRINT",FACE,{"disambiguationData":[TD([[makeQuery(id+"F1.imprint","IMPRINT",EDGE,{"derivedFrom":sQuery(id+"F1.wireOp",EDGE,"c9cc7f5d-6211-4dc9-b41b-aaae2feddd97.4.0.0")}),-1.0]])]});
            var Q12;
            Q12=makeQuery(id+"F1.imprint","IMPRINT",FACE,{"disambiguationData":[TD([[makeQuery(id+"F1.imprint","IMPRINT",EDGE,{"derivedFrom":sQuery(id+"F1.wireOp",EDGE,"c9cc7f5d-6211-4dc9-b41b-aaae2feddd97.5.0.0")}),-1.0]])]});
            var Q13;
            {var subQ0=sQuery(id+"F1.wireOp",EDGE,"e9a3ff06-c462-4903-9302-cb255ffcaa57.0.5.0");Q13=makeQuery(id+"F1.imprint","IMPRINT",FACE,{"disambiguationData":[TD([[makeQuery(id+"F1.imprint","IMPRINT",EDGE,{"derivedFrom":subQ0}),1.0]])]});}
            var Q14;
            {var subQ0=sQuery(id+"F1.wireOp",EDGE,"E0.top");Q14=makeQuery(id+"F1.imprint","IMPRINT",FACE,{"disambiguationData":[TD([[makeQuery(id+"F1.imprint","IMPRINT",EDGE,{"derivedFrom":subQ0}),1.0]])]});}
            var Q15;
            {var subQ0=sQuery(id+"F1.wireOp",EDGE,"zuuYGtIx-YfND-we87-dVk1-2TNHSHCjCdNj.top");Q15=makeQuery(id+"F1.imprint","IMPRINT",FACE,{"disambiguationData":[TD([[makeQuery(id+"F1.imprint","IMPRINT",EDGE,{"derivedFrom":subQ0}),1.0]])]});}
            var Q16;
            Q16=makeQuery(id+"F1.imprint","IMPRINT",FACE,{"disambiguationData":[TD([[makeQuery(id+"F1.imprint","IMPRINT",EDGE,{"derivedFrom":sQuery(id+"F1.wireOp",EDGE,"RaYTgRfS-HCax-OzBH-qsnV-oxM8qn66qDHo.bottom")}),-1.0]])]});
            var Q17;
            Q17=makeQuery(id+"F1.imprint","IMPRINT",FACE,{"disambiguationData":[TD([[makeQuery(id+"F1.imprint","IMPRINT",EDGE,{"derivedFrom":sQuery(id+"F1.wireOp",EDGE,"A2z6aU3x-cg6c-CzpY-Q7PS-y1Ii9rqkyWUI.bottom")}),-1.0]])]});
            var Q18;
            Q18=makeQuery(id+"F1.imprint","IMPRINT",FACE,{"disambiguationData":[TD([[makeQuery(id+"F1.imprint","IMPRINT",EDGE,{"derivedFrom":sQuery(id+"F1.wireOp",EDGE,"7ee9f5a2-2083-4d3d-b315-0f95102f96d621.MirrorC")}),1.0]])]});
            var Q19;
            Q19=makeQuery(id+"F1.imprint","IMPRINT",FACE,{"disambiguationData":[TD([[makeQuery(id+"F1.imprint","IMPRINT",EDGE,{"derivedFrom":sQuery(id+"F1.wireOp",EDGE,"7ee9f5a2-2083-4d3d-b315-0f95102f96d60.MirrorCS")}),1.0]])]});
            var Q20;
            {var subQ8=sQuery(id+"F1.wireOp",EDGE,"3cc9daea-cbba-44d1-9671-21d01c85290615.MirrorCS");Q20=makeQuery(id+"F1.imprint","IMPRINT",FACE,{"disambiguationData":[TD([[makeQuery(id+"F1.imprint","IMPRINT",EDGE,{"derivedFrom":subQ8}),-1.0]])]});}
            var Q21;
            Q21=makeQuery(id+"F1.imprint","IMPRINT",FACE,{"disambiguationData":[TD([[makeQuery(id+"F1.imprint","IMPRINT",EDGE,{"derivedFrom":sQuery(id+"F1.wireOp",EDGE,"3cc9daea-cbba-44d1-9671-21d01c85290657.MirrorCS")}),1.0]])]});
            var Q22;
            Q22=makeQuery(id+"F1.imprint","IMPRINT",FACE,{"disambiguationData":[TD([[makeQuery(id+"F1.imprint","IMPRINT",EDGE,{"derivedFrom":sQuery(id+"F1.wireOp",EDGE,"3cc9daea-cbba-44d1-9671-21d01c85290645.MirrorCS")}),1.0]])]});
            var Q23;
            Q23=makeQuery(id+"F1.imprint","IMPRINT",FACE,{"disambiguationData":[TD([[makeQuery(id+"F1.imprint","IMPRINT",EDGE,{"derivedFrom":sQuery(id+"F1.wireOp",EDGE,"3cc9daea-cbba-44d1-9671-21d01c85290633.MirrorC")}),1.0]])]});
            var Q24;
            Q24=makeQuery(id+"F1.imprint","IMPRINT",FACE,{"disambiguationData":[TD([[makeQuery(id+"F1.imprint","IMPRINT",EDGE,{"derivedFrom":sQuery(id+"F1.wireOp",EDGE,"3cc9daea-cbba-44d1-9671-21d01c85290625.MirrorCS")}),-1.0]])]});
            var Q25;
            {var subQ1=sQuery(id+"F1.wireOp",EDGE,"3cc9daea-cbba-44d1-9671-21d01c85290614.MirrorCS");Q25=makeQuery(id+"F1.imprint","IMPRINT",FACE,{"disambiguationData":[TD([[makeQuery(id+"F1.imprint","IMPRINT",EDGE,{"derivedFrom":subQ1}),1.0]])]});}
            var Q26;
            {var subQ1=sQuery(id+"F1.wireOp",EDGE,"3cc9daea-cbba-44d1-9671-21d01c85290616.MirrorCS");var subQ3=sQuery(id+"F1.wireOp",EDGE,"3cc9daea-cbba-44d1-9671-21d01c85290618.MirrorCS");var subQ4=makeQuery(id+"F1.imprint","INTERSECT",VERTEX,{"derivedFrom":[subQ1,subQ3]});Q26=makeQuery(id+"F1.imprint","IMPRINT",FACE,{"disambiguationData":[TD([[makeQuery(id+"F1.imprint","IMPRINT",EDGE,{"disambiguationData":[TD([[subQ4,-1.0]])],"derivedFrom":subQ3}),1.0]])]});}
            var Q27;
            {var subQ2=sQuery(id+"F1.wireOp",EDGE,"3cc9daea-cbba-44d1-9671-21d01c85290632.MirrorCS");Q27=makeQuery(id+"F1.imprint","IMPRINT",FACE,{"disambiguationData":[TD([[makeQuery(id+"F1.imprint","IMPRINT",EDGE,{"derivedFrom":subQ2}),-1.0]])]});}
            var Q28;
            {var subQ2=sQuery(id+"F1.wireOp",EDGE,"3cc9daea-cbba-44d1-9671-21d01c85290615.MirrorCS");Q28=makeQuery(id+"F1.imprint","IMPRINT",FACE,{"disambiguationData":[TD([[makeQuery(id+"F1.imprint","IMPRINT",EDGE,{"derivedFrom":subQ2}),1.0]])]});}
            var Q29;
            Q29=makeQuery(id+"F1.imprint","IMPRINT",FACE,{"disambiguationData":[TD([[makeQuery(id+"F1.imprint","IMPRINT",EDGE,{"derivedFrom":sQuery(id+"F1.wireOp",EDGE,"7ee9f5a2-2083-4d3d-b315-0f95102f96d68.MirrorCS")}),1.0]])]});
            var Q30;
            Q30=makeQuery(id+"F1.imprint","IMPRINT",FACE,{"disambiguationData":[TD([[makeQuery(id+"F1.imprint","IMPRINT",EDGE,{"derivedFrom":sQuery(id+"F1.wireOp",EDGE,"7ee9f5a2-2083-4d3d-b315-0f95102f96d66.MirrorCS")}),1.0]])]});
            var Q31;
            {var subQ1=sQuery(id+"F1.wireOp",EDGE,"Ql8xjKSZ-osiJ-ou1O-RUti-zKqZGMklHdmG.bottom");Q31=makeQuery(id+"F1.imprint","IMPRINT",FACE,{"disambiguationData":[TD([[makeQuery(id+"F1.imprint","IMPRINT",EDGE,{"derivedFrom":subQ1}),-1.0]])]});}
            var Q32;
            {var subQ1=sQuery(id+"F1.wireOp",EDGE,"vNJjCRz3-f4OO-4W7b-yauL-aWNgJRgR4KzO.bottom");Q32=makeQuery(id+"F1.imprint","IMPRINT",FACE,{"disambiguationData":[TD([[makeQuery(id+"F1.imprint","IMPRINT",EDGE,{"derivedFrom":subQ1}),1.0]])]});}
            var Q33;
            {var subQ0=sQuery(id+"F1.wireOp",EDGE,"RaYTgRfS-HCax-OzBH-qsnV-oxM8qn66qDHo.top");Q33=makeQuery(id+"F1.imprint","IMPRINT",FACE,{"disambiguationData":[TD([[makeQuery(id+"F1.imprint","IMPRINT",EDGE,{"derivedFrom":subQ0}),1.0]])]});}
            var Q34;
            Q34=makeQuery(id+"F1.imprint","IMPRINT",FACE,{"disambiguationData":[TD([[makeQuery(id+"F1.imprint","IMPRINT",EDGE,{"derivedFrom":sQuery(id+"F1.wireOp",EDGE,"MePqlvqW-R92V-4SML-vUzJ-x8LzeLdQ50hA.bottom")}),-1.0]])]});
            var Q35;
            Q35=makeQuery(id+"F1.imprint","IMPRINT",FACE,{"disambiguationData":[TD([[makeQuery(id+"F1.imprint","IMPRINT",EDGE,{"derivedFrom":sQuery(id+"F1.wireOp",EDGE,"eToSEdLw-ZPEH-Me9I-LjQH-tnaRYInkmE1b.bottom")}),1.0]])]});
            var Q36;
            Q36=makeQuery(id+"F1.imprint","IMPRINT",FACE,{"disambiguationData":[TD([[makeQuery(id+"F1.imprint","IMPRINT",EDGE,{"derivedFrom":sQuery(id+"F1.wireOp",EDGE,"7ee9f5a2-2083-4d3d-b315-0f95102f96d64.MirrorCS")}),-1.0]])]});
            var Q37;
            Q37=makeQuery(id+"F1.imprint","IMPRINT",FACE,{"disambiguationData":[TD([[makeQuery(id+"F1.imprint","IMPRINT",EDGE,{"derivedFrom":sQuery(id+"F1.wireOp",EDGE,"7ee9f5a2-2083-4d3d-b315-0f95102f96d62.MirrorCS")}),1.0]])]});
            var Q38;
            Q38=makeQuery(id+"F1.imprint","IMPRINT",FACE,{"disambiguationData":[TD([[makeQuery(id+"F1.imprint","IMPRINT",EDGE,{"derivedFrom":sQuery(id+"F1.wireOp",EDGE,"3cc9daea-cbba-44d1-9671-21d01c85290613.MirrorCS")}),1.0]])]});
            var Q39;
            Q39=makeQuery(id+"F1.imprint","IMPRINT",FACE,{"disambiguationData":[TD([[makeQuery(id+"F1.imprint","IMPRINT",EDGE,{"derivedFrom":sQuery(id+"F1.wireOp",EDGE,"3cc9daea-cbba-44d1-9671-21d01c85290642.MirrorCS")}),-1.0]])]});
            var Q40;
            Q40=makeQuery(id+"F1.imprint","IMPRINT",FACE,{"disambiguationData":[TD([[makeQuery(id+"F1.imprint","IMPRINT",EDGE,{"derivedFrom":sQuery(id+"F1.wireOp",EDGE,"3cc9daea-cbba-44d1-9671-21d01c85290620.MirrorCS")}),-1.0]])]});
            var Q41;
            Q41=makeQuery(id+"F1.imprint","IMPRINT",FACE,{"disambiguationData":[TD([[makeQuery(id+"F1.imprint","IMPRINT",EDGE,{"derivedFrom":sQuery(id+"F1.wireOp",EDGE,"3cc9daea-cbba-44d1-9671-21d01c85290621.MirrorCS")}),-1.0]])]});
            var Q42;
            Q42=makeQuery(id+"F1.imprint","IMPRINT",FACE,{"disambiguationData":[TD([[makeQuery(id+"F1.imprint","IMPRINT",EDGE,{"derivedFrom":sQuery(id+"F1.wireOp",EDGE,"8i7omnKA-XiQc-A4SL-4TcC-43kh4ndWTDuy.bottom")}),-1.0]])]});
            var Q43;
            {var subQ0=sQuery(id+"F1.wireOp",EDGE,"7ee9f5a2-2083-4d3d-b315-0f95102f96d610.MirrorCS");Q43=makeQuery(id+"F1.imprint","IMPRINT",FACE,{"disambiguationData":[TD([[makeQuery(id+"F1.imprint","IMPRINT",EDGE,{"derivedFrom":subQ0}),1.0]])]});}
            var Q44;
            {var subQ0=sQuery(id+"F1.wireOp",EDGE,"7ee9f5a2-2083-4d3d-b315-0f95102f96d65.MirrorCS");Q44=makeQuery(id+"F1.imprint","IMPRINT",FACE,{"disambiguationData":[TD([[makeQuery(id+"F1.imprint","IMPRINT",EDGE,{"derivedFrom":subQ0}),1.0]])]});}
            var Q45;
            {var subQ0=sQuery(id+"F1.wireOp",EDGE,"3cc9daea-cbba-44d1-9671-21d01c85290626.MirrorCS");Q45=makeQuery(id+"F1.imprint","IMPRINT",FACE,{"disambiguationData":[TD([[makeQuery(id+"F1.imprint","IMPRINT",EDGE,{"derivedFrom":subQ0}),-1.0]])]});}
            var Q46;
            {var subQ0=sQuery(id+"F1.wireOp",EDGE,"3cc9daea-cbba-44d1-9671-21d01c8529068.MirrorCS");Q46=makeQuery(id+"F1.imprint","IMPRINT",FACE,{"disambiguationData":[TD([[makeQuery(id+"F1.imprint","IMPRINT",EDGE,{"derivedFrom":subQ0}),1.0]])]});}
            var Q47;
            {var subQ0=sQuery(id+"F1.wireOp",EDGE,"3cc9daea-cbba-44d1-9671-21d01c85290640.MirrorCS");Q47=makeQuery(id+"F1.imprint","IMPRINT",FACE,{"disambiguationData":[TD([[makeQuery(id+"F1.imprint","IMPRINT",EDGE,{"derivedFrom":subQ0}),1.0]])]});}
            var Q48;
            {var subQ0=sQuery(id+"F1.wireOp",EDGE,"3cc9daea-cbba-44d1-9671-21d01c85290612.MirrorCS");Q48=makeQuery(id+"F1.imprint","IMPRINT",FACE,{"disambiguationData":[TD([[makeQuery(id+"F1.imprint","IMPRINT",EDGE,{"derivedFrom":subQ0}),-1.0]])]});}
            var Q49;
            Q49=makeQuery(id+"F1.imprint","IMPRINT",FACE,{"disambiguationData":[TD([[makeQuery(id+"F1.imprint","IMPRINT",EDGE,{"derivedFrom":sQuery(id+"F1.wireOp",EDGE,"pkzA8YXS-147m-h1o3-BIs2-CFvluc7HSHoC.bottom")}),1.0]])]});
            var Q50;
            {var subQ5=sQuery(id+"F1.wireOp",EDGE,"43f020bf-c188-477f-bb01-5622551f1bd82.MirrorCS");Q50=makeQuery(id+"F1.imprint","IMPRINT",FACE,{"disambiguationData":[TD([[makeQuery(id+"F1.imprint","IMPRINT",EDGE,{"derivedFrom":subQ5}),1.0]])]});}
            var Q51;
            Q51=makeQuery(id+"F1.imprint","IMPRINT",FACE,{"disambiguationData":[TD([[makeQuery(id+"F1.imprint","IMPRINT",EDGE,{"derivedFrom":sQuery(id+"F1.wireOp",EDGE,"FgWoepQM-oAc9-YKjo-rVyh-H2xzB4l6eYAx.bottom")}),-1.0]])]});
            var Q52;
            Q52=makeQuery(id+"F1.imprint","IMPRINT",FACE,{"disambiguationData":[TD([[makeQuery(id+"F1.imprint","IMPRINT",EDGE,{"derivedFrom":sQuery(id+"F1.wireOp",EDGE,"nsbAEkxb-gdlj-1fSG-6ZRn-gvIsFKBOcmSa.top")}),1.0]])]});
            var Q53;
            Q53=makeQuery(id+"F1.imprint","IMPRINT",FACE,{"disambiguationData":[TD([[makeQuery(id+"F1.imprint","IMPRINT",EDGE,{"derivedFrom":sQuery(id+"F1.wireOp",EDGE,"7ab01751-0d8d-4895-afa0-6445531c586e.1.0.1")}),-1.0]])]});
            var Q54;
            Q54=makeQuery(id+"F1.imprint","IMPRINT",FACE,{"disambiguationData":[TD([[makeQuery(id+"F1.imprint","IMPRINT",EDGE,{"derivedFrom":sQuery(id+"F1.wireOp",EDGE,"7ab01751-0d8d-4895-afa0-6445531c586e.2.0.1")}),-1.0]])]});
            var Q55;
            Q55=makeQuery(id+"F1.imprint","IMPRINT",FACE,{"disambiguationData":[TD([[makeQuery(id+"F1.imprint","IMPRINT",EDGE,{"derivedFrom":sQuery(id+"F1.wireOp",EDGE,"7ab01751-0d8d-4895-afa0-6445531c586e.3.0.1")}),-1.0]])]});
            var Q56;
            Q56=makeQuery(id+"F1.imprint","IMPRINT",FACE,{"disambiguationData":[TD([[makeQuery(id+"F1.imprint","IMPRINT",EDGE,{"derivedFrom":sQuery(id+"F1.wireOp",EDGE,"7ab01751-0d8d-4895-afa0-6445531c586e.4.0.1")}),-1.0]])]});
            var Q57;
            Q57=makeQuery(id+"F1.imprint","IMPRINT",FACE,{"disambiguationData":[TD([[makeQuery(id+"F1.imprint","IMPRINT",EDGE,{"derivedFrom":sQuery(id+"F1.wireOp",EDGE,"7ab01751-0d8d-4895-afa0-6445531c586e.5.0.1")}),-1.0]])]});
            var Q58;
            Q58=makeQuery(id+"F1.imprint","IMPRINT",FACE,{"disambiguationData":[TD([[makeQuery(id+"F1.imprint","IMPRINT",EDGE,{"derivedFrom":sQuery(id+"F1.wireOp",EDGE,"49cf5ac7-3a91-41c2-95b4-914cce5436a2.1.6.0")}),-1.0]])]});
            var Q59;
            {var subQ2=sQuery(id+"F1.wireOp",EDGE,"Y7vdvrbU-9VXp-oTm6-BqFg-j6OfKwPQvjlB");Q59=makeQuery(id+"F1.imprint","IMPRINT",FACE,{"disambiguationData":[TD([[makeQuery(id+"F1.imprint","IMPRINT",EDGE,{"derivedFrom":subQ2}),-1.0]])]});}
            var Q60;
            {var subQ9=sQuery(id+"F1.wireOp",EDGE,"E5.top");Q60=makeQuery(id+"F1.imprint","IMPRINT",FACE,{"disambiguationData":[TD([[makeQuery(id+"F1.imprint","IMPRINT",EDGE,{"derivedFrom":subQ9}),1.0]])]});}
            var Q61;
            {var subQ0=sQuery(id+"F1.wireOp",EDGE,"E37.bottom");Q61=makeQuery(id+"F1.imprint","IMPRINT",FACE,{"disambiguationData":[TD([[makeQuery(id+"F1.imprint","IMPRINT",EDGE,{"derivedFrom":subQ0}),-1.0]])]});}
            var Q62;
            {var subQ9=sQuery(id+"F1.wireOp",EDGE,"E50.top");Q62=makeQuery(id+"F1.imprint","IMPRINT",FACE,{"disambiguationData":[TD([[makeQuery(id+"F1.imprint","IMPRINT",EDGE,{"derivedFrom":subQ9}),-1.0]])]});}
            var Q63;
            Q63=makeQuery(id+"F1.imprint","IMPRINT",FACE,{"disambiguationData":[TD([[makeQuery(id+"F1.imprint","IMPRINT",EDGE,{"derivedFrom":sQuery(id+"F1.wireOp",EDGE,"E38.MirrorCS")}),-1.0]])]});
            var Q64;
            Q64=makeQuery(id+"F1.imprint","IMPRINT",FACE,{"disambiguationData":[TD([[makeQuery(id+"F1.imprint","IMPRINT",EDGE,{"derivedFrom":sQuery(id+"F1.wireOp",EDGE,"E53.bottom")}),-1.0]])]});
            var Q65;
            Q65=makeQuery(id+"F1.imprint","IMPRINT",FACE,{"disambiguationData":[TD([[makeQuery(id+"F1.imprint","IMPRINT",EDGE,{"derivedFrom":sQuery(id+"F1.wireOp",EDGE,"E72.MirrorCS")}),-1.0]])]});
            var Q66;
            Q66=makeQuery(id+"F1.imprint","IMPRINT",FACE,{"disambiguationData":[TD([[makeQuery(id+"F1.imprint","IMPRINT",EDGE,{"derivedFrom":sQuery(id+"F1.wireOp",EDGE,"E56.MirrorCS")}),-1.0]])]});
            var Q67;
            {var subQ12=sQuery(id+"F1.wireOp",EDGE,"E68.MirrorCS");Q67=makeQuery(id+"F1.imprint","IMPRINT",FACE,{"disambiguationData":[TD([[makeQuery(id+"F1.imprint","IMPRINT",EDGE,{"derivedFrom":subQ12}),1.0]])]});}
            var Q68;
            {var subQ0=sQuery(id+"F1.wireOp",EDGE,"E55.MirrorCS");Q68=makeQuery(id+"F1.imprint","IMPRINT",FACE,{"disambiguationData":[TD([[makeQuery(id+"F1.imprint","IMPRINT",EDGE,{"derivedFrom":subQ0}),1.0]])]});}
            var Q69;
            {var subQ0=sQuery(id+"F1.wireOp",EDGE,"E36.bottom");Q69=makeQuery(id+"F1.imprint","IMPRINT",FACE,{"disambiguationData":[TD([[makeQuery(id+"F1.imprint","IMPRINT",EDGE,{"derivedFrom":subQ0}),-1.0]])]});}
            var Q70;
            Q70=makeQuery(id+"F1.imprint","IMPRINT",FACE,{"disambiguationData":[TD([[makeQuery(id+"F1.imprint","IMPRINT",EDGE,{"derivedFrom":sQuery(id+"F1.wireOp",EDGE,"E42.MirrorCS")}),-1.0]])]});
            var Q71;
            {var subQ0=sQuery(id+"F1.wireOp",EDGE,"E65.MirrorCS");Q71=makeQuery(id+"F1.imprint","IMPRINT",FACE,{"disambiguationData":[TD([[makeQuery(id+"F1.imprint","IMPRINT",EDGE,{"derivedFrom":subQ0}),1.0]])]});}
            var Q72;
            {var subQ0=sQuery(id+"F1.wireOp",EDGE,"E59.MirrorCS");Q72=makeQuery(id+"F1.imprint","IMPRINT",FACE,{"disambiguationData":[TD([[makeQuery(id+"F1.imprint","IMPRINT",EDGE,{"derivedFrom":subQ0}),-1.0]])]});}
            var Q73;
            {var subQ2=sQuery(id+"F1.wireOp",EDGE,"E50.bottom");Q73=makeQuery(id+"F1.imprint","IMPRINT",FACE,{"disambiguationData":[TD([[makeQuery(id+"F1.imprint","IMPRINT",EDGE,{"derivedFrom":subQ2}),1.0]])]});}
            var Q74;
            {var subQ1=sQuery(id+"F1.wireOp",EDGE,"E34.bottom");Q74=makeQuery(id+"F1.imprint","IMPRINT",FACE,{"disambiguationData":[TD([[makeQuery(id+"F1.imprint","IMPRINT",EDGE,{"derivedFrom":subQ1}),1.0]])]});}
            var Q75;
            {var subQ0=sQuery(id+"F1.wireOp",EDGE,"E58.MirrorCS");Q75=makeQuery(id+"F1.imprint","IMPRINT",FACE,{"disambiguationData":[TD([[makeQuery(id+"F1.imprint","IMPRINT",EDGE,{"derivedFrom":subQ0}),-1.0]])]});}
            var Q76;
            {var subQ0=sQuery(id+"F1.wireOp",EDGE,"E57.MirrorCS");Q76=makeQuery(id+"F1.imprint","IMPRINT",FACE,{"disambiguationData":[TD([[makeQuery(id+"F1.imprint","IMPRINT",EDGE,{"derivedFrom":subQ0}),1.0]])]});}
            var Q77;
            {var subQ3=sQuery(id+"F1.wireOp",EDGE,"E32");Q77=makeQuery(id+"F1.imprint","IMPRINT",FACE,{"disambiguationData":[TD([[makeQuery(id+"F1.imprint","IMPRINT",EDGE,{"derivedFrom":subQ3}),1.0]])]});}
            var Q78;
            Q78=makeQuery(id+"F1.imprint","IMPRINT",FACE,{"disambiguationData":[TD([[makeQuery(id+"F1.imprint","IMPRINT",EDGE,{"derivedFrom":sQuery(id+"F1.wireOp",EDGE,"E46.MirrorCS")}),1.0]])]});
            var Q79;
            Q79=makeQuery(id+"F1.imprint","IMPRINT",FACE,{"disambiguationData":[TD([[makeQuery(id+"F1.imprint","IMPRINT",EDGE,{"derivedFrom":sQuery(id+"F1.wireOp",EDGE,"E91.bottom")}),-1.0]])]});
            var Q80;
            Q80=makeQuery(id+"F1.imprint","IMPRINT",FACE,{"disambiguationData":[TD([[makeQuery(id+"F1.imprint","IMPRINT",EDGE,{"derivedFrom":sQuery(id+"F1.wireOp",EDGE,"E91.left")}),-1.0]])]});
            var Q81;
            Q81=makeQuery(id+"F1.imprint","IMPRINT",FACE,{"disambiguationData":[TD([[makeQuery(id+"F1.imprint","IMPRINT",EDGE,{"derivedFrom":sQuery(id+"F1.wireOp",EDGE,"E91.right")}),1.0]])]});
            var Q82;
            {var subQ9=sQuery(id+"F1.wireOp",EDGE,"aa94eb73-4e7f-4a9c-8df9-c293ded4868a13.MirrorCS");Q82=makeQuery(id+"F1.imprint","IMPRINT",FACE,{"disambiguationData":[TD([[makeQuery(id+"F1.imprint","IMPRINT",EDGE,{"derivedFrom":subQ9}),-1.0]])]});}
            var Q83;
            {var subQ2=sQuery(id+"F1.wireOp",EDGE,"aa94eb73-4e7f-4a9c-8df9-c293ded4868a35.MirrorCS");Q83=makeQuery(id+"F1.imprint","IMPRINT",FACE,{"disambiguationData":[TD([[makeQuery(id+"F1.imprint","IMPRINT",EDGE,{"derivedFrom":subQ2}),1.0]])]});}
            var Q84;
            {var subQ1=sQuery(id+"F1.wireOp",EDGE,"aa94eb73-4e7f-4a9c-8df9-c293ded4868a31.MirrorCS");Q84=makeQuery(id+"F1.imprint","IMPRINT",FACE,{"disambiguationData":[TD([[makeQuery(id+"F1.imprint","IMPRINT",EDGE,{"derivedFrom":subQ1}),-1.0]])]});}
            var Q85;
            {var subQ1=sQuery(id+"F1.wireOp",EDGE,"aa94eb73-4e7f-4a9c-8df9-c293ded4868a39.MirrorCS");Q85=makeQuery(id+"F1.imprint","IMPRINT",FACE,{"disambiguationData":[TD([[makeQuery(id+"F1.imprint","IMPRINT",EDGE,{"derivedFrom":subQ1}),-1.0]])]});}
            var Q86;
            Q86=makeQuery(id+"F1.imprint","IMPRINT",FACE,{"disambiguationData":[TD([[makeQuery(id+"F1.imprint","IMPRINT",EDGE,{"derivedFrom":sQuery(id+"F1.wireOp",EDGE,"aa94eb73-4e7f-4a9c-8df9-c293ded4868a33.MirrorC")}),1.0]])]});
            var Q87;
            Q87=makeQuery(id+"F1.imprint","IMPRINT",FACE,{"disambiguationData":[TD([[makeQuery(id+"F1.imprint","IMPRINT",EDGE,{"derivedFrom":sQuery(id+"F1.wireOp",EDGE,"aa94eb73-4e7f-4a9c-8df9-c293ded4868a52.MirrorC")}),1.0]])]});
            var Q88;
            {var subQ5=sQuery(id+"F1.wireOp",EDGE,"aa94eb73-4e7f-4a9c-8df9-c293ded4868a3.MirrorCS");Q88=makeQuery(id+"F1.imprint","IMPRINT",FACE,{"disambiguationData":[TD([[makeQuery(id+"F1.imprint","IMPRINT",EDGE,{"derivedFrom":subQ5}),-1.0]])]});}
            var Q89;
            {var subQ5=sQuery(id+"F1.wireOp",EDGE,"aa94eb73-4e7f-4a9c-8df9-c293ded4868a24.MirrorCS");Q89=makeQuery(id+"F1.imprint","IMPRINT",FACE,{"disambiguationData":[TD([[makeQuery(id+"F1.imprint","IMPRINT",EDGE,{"derivedFrom":subQ5}),-1.0]])]});}
            var Q90;
            {var subQ5=sQuery(id+"F1.wireOp",EDGE,"aa94eb73-4e7f-4a9c-8df9-c293ded4868a4.MirrorCS");Q90=makeQuery(id+"F1.imprint","IMPRINT",FACE,{"disambiguationData":[TD([[makeQuery(id+"F1.imprint","IMPRINT",EDGE,{"derivedFrom":subQ5}),1.0]])]});}
            var Q91;
            {var subQ0=sQuery(id+"F1.wireOp",EDGE,"E15");Q91=makeQuery(id+"F1.imprint","IMPRINT",FACE,{"disambiguationData":[TD([[makeQuery(id+"F1.imprint","IMPRINT",EDGE,{"derivedFrom":subQ0}),1.0]])]});}
            var Q92;
            {var subQ0=sQuery(id+"F1.wireOp",EDGE,"E16.1.0.0");Q92=makeQuery(id+"F1.imprint","IMPRINT",FACE,{"disambiguationData":[TD([[makeQuery(id+"F1.imprint","IMPRINT",EDGE,{"derivedFrom":subQ0}),1.0]])]});}
            var Q93;
            {var subQ0=sQuery(id+"F1.wireOp",EDGE,"E16.2.0.0");Q93=makeQuery(id+"F1.imprint","IMPRINT",FACE,{"disambiguationData":[TD([[makeQuery(id+"F1.imprint","IMPRINT",EDGE,{"derivedFrom":subQ0}),1.0]])]});}
            var Q94;
            {var subQ0=sQuery(id+"F1.wireOp",EDGE,"E16.3.0.0");Q94=makeQuery(id+"F1.imprint","IMPRINT",FACE,{"disambiguationData":[TD([[makeQuery(id+"F1.imprint","IMPRINT",EDGE,{"derivedFrom":subQ0}),1.0]])]});}
            var Q95;
            {var subQ0=sQuery(id+"F1.wireOp",EDGE,"E16.4.0.0");Q95=makeQuery(id+"F1.imprint","IMPRINT",FACE,{"disambiguationData":[TD([[makeQuery(id+"F1.imprint","IMPRINT",EDGE,{"derivedFrom":subQ0}),1.0]])]});}
            extrude(context, id + "F2", {"entities" : qUnion([Q0, Q1, Q2, Q3, Q4, Q5, Q6, Q7, Q8, Q9, Q10, Q11, Q12, Q13, Q14, Q15, Q16, Q17, Q18, Q19, Q20, Q21, Q22, Q23, Q24, Q25, Q26, Q27, Q28, Q29, Q30, Q31, Q32, Q33, Q34, Q35, Q36, Q37, Q38, Q39, Q40, Q41, Q42, Q43, Q44, Q45, Q46, Q47, Q48, Q49, Q50, Q51, Q52, Q53, Q54, Q55, Q56, Q57, Q58, Q59, Q60, Q61, Q62, Q63, Q64, Q65, Q66, Q67, Q68, Q69, Q70, Q71, Q72, Q73, Q74, Q75, Q76, Q77, Q78, Q79, Q80, Q81, Q82, Q83, Q84, Q85, Q86, Q87, Q88, Q89, Q90, Q91, Q92, Q93, Q94, Q95]), "depth" : (getVariable(context, 'Thickness')) * mm});
        }
        {
            var Q0;
            Q0=makeQuery(id+"F1.imprint","IMPRINT",FACE,{"disambiguationData":[TD([[makeQuery(id+"F1.imprint","IMPRINT",EDGE,{"derivedFrom":sQuery(id+"F1.wireOp",EDGE,"63688b75-6c1a-4b18-8993-3e2f64380d1d.0.startCap")}),1.0]])]});
            var Q1;
            {var subQ0=sQuery(id+"F1.wireOp",EDGE,"E14");Q1=makeQuery(id+"F1.imprint","IMPRINT",FACE,{"disambiguationData":[TD([[makeQuery(id+"F1.imprint","IMPRINT",EDGE,{"derivedFrom":subQ0}),1.0]])]});}
            var Q2;
            {var subQ0=sQuery(id+"F1.wireOp",EDGE,"E16.1.0.0");Q2=makeQuery(id+"F1.imprint","IMPRINT",FACE,{"disambiguationData":[TD([[makeQuery(id+"F1.imprint","IMPRINT",EDGE,{"derivedFrom":subQ0}),-1.0]])]});}
            var Q3;
            {var subQ0=sQuery(id+"F1.wireOp",EDGE,"E16.2.0.0");Q3=makeQuery(id+"F1.imprint","IMPRINT",FACE,{"disambiguationData":[TD([[makeQuery(id+"F1.imprint","IMPRINT",EDGE,{"derivedFrom":subQ0}),-1.0]])]});}
            var Q4;
            {var subQ0=sQuery(id+"F1.wireOp",EDGE,"E16.3.0.0");Q4=makeQuery(id+"F1.imprint","IMPRINT",FACE,{"disambiguationData":[TD([[makeQuery(id+"F1.imprint","IMPRINT",EDGE,{"derivedFrom":subQ0}),-1.0]])]});}
            var Q5;
            {var subQ0=sQuery(id+"F1.wireOp",EDGE,"E16.4.0.0");Q5=makeQuery(id+"F1.imprint","IMPRINT",FACE,{"disambiguationData":[TD([[makeQuery(id+"F1.imprint","IMPRINT",EDGE,{"derivedFrom":subQ0}),-1.0]])]});}
            var Q6;
            {var subQ0=sQuery(id+"F1.wireOp",EDGE,"E16.5.0.0");Q6=makeQuery(id+"F1.imprint","IMPRINT",FACE,{"disambiguationData":[TD([[makeQuery(id+"F1.imprint","IMPRINT",EDGE,{"derivedFrom":subQ0}),-1.0]])]});}
            var Q7;
            {var subQ0=sQuery(id+"F1.wireOp",EDGE,"E16.6.0.0");Q7=makeQuery(id+"F1.imprint","IMPRINT",FACE,{"disambiguationData":[TD([[makeQuery(id+"F1.imprint","IMPRINT",EDGE,{"derivedFrom":subQ0}),-1.0]])]});}
            var Q8;
            {var subQ0=sQuery(id+"F1.wireOp",EDGE,"aa94eb73-4e7f-4a9c-8df9-c293ded4868a79.MirrorCS");Q8=makeQuery(id+"F1.imprint","IMPRINT",FACE,{"disambiguationData":[TD([[makeQuery(id+"F1.imprint","IMPRINT",EDGE,{"derivedFrom":subQ0}),-1.0]])]});}
            var Q9;
            {var subQ0=sQuery(id+"F1.wireOp",EDGE,"aa94eb73-4e7f-4a9c-8df9-c293ded4868a31.MirrorCS");Q9=makeQuery(id+"F1.imprint","IMPRINT",FACE,{"disambiguationData":[TD([[makeQuery(id+"F1.imprint","IMPRINT",EDGE,{"derivedFrom":subQ0}),1.0]])]});}
            var Q10;
            {var subQ0=sQuery(id+"F1.wireOp",EDGE,"aa94eb73-4e7f-4a9c-8df9-c293ded4868a39.MirrorCS");Q10=makeQuery(id+"F1.imprint","IMPRINT",FACE,{"disambiguationData":[TD([[makeQuery(id+"F1.imprint","IMPRINT",EDGE,{"derivedFrom":subQ0}),1.0]])]});}
            var Q11;
            {var subQ0=sQuery(id+"F1.wireOp",EDGE,"aa94eb73-4e7f-4a9c-8df9-c293ded4868a46.MirrorCS");Q11=makeQuery(id+"F1.imprint","IMPRINT",FACE,{"disambiguationData":[TD([[makeQuery(id+"F1.imprint","IMPRINT",EDGE,{"derivedFrom":subQ0}),1.0]])]});}
            var Q12;
            {var subQ0=sQuery(id+"F1.wireOp",EDGE,"aa94eb73-4e7f-4a9c-8df9-c293ded4868a54.MirrorCS");Q12=makeQuery(id+"F1.imprint","IMPRINT",FACE,{"disambiguationData":[TD([[makeQuery(id+"F1.imprint","IMPRINT",EDGE,{"derivedFrom":subQ0}),1.0]])]});}
            var Q13;
            {var subQ0=sQuery(id+"F1.wireOp",EDGE,"aa94eb73-4e7f-4a9c-8df9-c293ded4868a60.MirrorCS");Q13=makeQuery(id+"F1.imprint","IMPRINT",FACE,{"disambiguationData":[TD([[makeQuery(id+"F1.imprint","IMPRINT",EDGE,{"derivedFrom":subQ0}),1.0]])]});}
            extrude(context, id + "F3", {"entities" : qUnion([Q0, Q1, Q2, Q3, Q4, Q5, Q6, Q7, Q8, Q9, Q10, Q11, Q12, Q13]), "operationType" : NewBodyOperationType.ADD, "depth" : (getVariable(context, 'Thickness') / 2) * mm});
        }
        {
            var Q0;
            {var subQ7=sQuery(id+"F1.wireOp",EDGE,"E18.right");Q0=makeQuery(id+"F1.imprint","IMPRINT",FACE,{"disambiguationData":[TD([[makeQuery(id+"F1.imprint","IMPRINT",EDGE,{"derivedFrom":subQ7}),1.0]])]});}
            var Q1;
            {var subQ5=sQuery(id+"F1.wireOp",EDGE,"E24.0");Q1=makeQuery(id+"F1.imprint","IMPRINT",FACE,{"disambiguationData":[TD([[makeQuery(id+"F1.imprint","IMPRINT",EDGE,{"derivedFrom":subQ5}),1.0]])]});}
            var Q2;
            {var subQ5=sQuery(id+"F1.wireOp",EDGE,"E23.0");Q2=makeQuery(id+"F1.imprint","IMPRINT",FACE,{"disambiguationData":[TD([[makeQuery(id+"F1.imprint","IMPRINT",EDGE,{"derivedFrom":subQ5}),-1.0]])]});}
            var Q3;
            {var subQ0=sQuery(id+"F1.wireOp",EDGE,"E19.1.0.0");var subQ1=sQuery(id+"F1.wireOp",EDGE,"E17.bottom");var subQ2=makeQuery(id+"F1.imprint","INTERSECT",VERTEX,{"derivedFrom":[subQ1,subQ0]});Q3=makeQuery(id+"F1.imprint","IMPRINT",FACE,{"disambiguationData":[TD([[makeQuery(id+"F1.imprint","IMPRINT",EDGE,{"disambiguationData":[TD([[subQ2,1.0]])],"derivedFrom":subQ1}),-1.0]])]});}
            var Q4;
            {var subQ5=sQuery(id+"F1.wireOp",EDGE,"E25.1.0.0");Q4=makeQuery(id+"F1.imprint","IMPRINT",FACE,{"disambiguationData":[TD([[makeQuery(id+"F1.imprint","IMPRINT",EDGE,{"derivedFrom":subQ5}),1.0]])]});}
            var Q5;
            {var subQ5=sQuery(id+"F1.wireOp",EDGE,"E25.1.0.1");Q5=makeQuery(id+"F1.imprint","IMPRINT",FACE,{"disambiguationData":[TD([[makeQuery(id+"F1.imprint","IMPRINT",EDGE,{"derivedFrom":subQ5}),-1.0]])]});}
            var Q6;
            {var subQ0=sQuery(id+"F1.wireOp",EDGE,"E19.2.0.0");var subQ7=sQuery(id+"F1.wireOp",EDGE,"E17.bottom");var subQ8=makeQuery(id+"F1.imprint","INTERSECT",VERTEX,{"derivedFrom":[subQ7,subQ0]});Q6=makeQuery(id+"F1.imprint","IMPRINT",FACE,{"disambiguationData":[TD([[makeQuery(id+"F1.imprint","IMPRINT",EDGE,{"disambiguationData":[TD([[subQ8,1.0]])],"derivedFrom":subQ7}),-1.0]])]});}
            var Q7;
            {var subQ5=sQuery(id+"F1.wireOp",EDGE,"E25.2.0.0");Q7=makeQuery(id+"F1.imprint","IMPRINT",FACE,{"disambiguationData":[TD([[makeQuery(id+"F1.imprint","IMPRINT",EDGE,{"derivedFrom":subQ5}),1.0]])]});}
            var Q8;
            {var subQ5=sQuery(id+"F1.wireOp",EDGE,"E25.2.0.1");Q8=makeQuery(id+"F1.imprint","IMPRINT",FACE,{"disambiguationData":[TD([[makeQuery(id+"F1.imprint","IMPRINT",EDGE,{"derivedFrom":subQ5}),-1.0]])]});}
            var Q9;
            {var subQ0=sQuery(id+"F1.wireOp",EDGE,"E19.3.0.0");var subQ3=sQuery(id+"F1.wireOp",EDGE,"E17.bottom");var subQ4=makeQuery(id+"F1.imprint","INTERSECT",VERTEX,{"derivedFrom":[subQ3,subQ0]});Q9=makeQuery(id+"F1.imprint","IMPRINT",FACE,{"disambiguationData":[TD([[makeQuery(id+"F1.imprint","IMPRINT",EDGE,{"disambiguationData":[TD([[subQ4,1.0]])],"derivedFrom":subQ3}),-1.0]])]});}
            var Q10;
            {var subQ5=sQuery(id+"F1.wireOp",EDGE,"E25.3.0.0");Q10=makeQuery(id+"F1.imprint","IMPRINT",FACE,{"disambiguationData":[TD([[makeQuery(id+"F1.imprint","IMPRINT",EDGE,{"derivedFrom":subQ5}),1.0]])]});}
            var Q11;
            {var subQ5=sQuery(id+"F1.wireOp",EDGE,"E25.3.0.1");Q11=makeQuery(id+"F1.imprint","IMPRINT",FACE,{"disambiguationData":[TD([[makeQuery(id+"F1.imprint","IMPRINT",EDGE,{"derivedFrom":subQ5}),-1.0]])]});}
            var Q12;
            {var subQ0=sQuery(id+"F1.wireOp",EDGE,"E19.4.0.0");var subQ3=sQuery(id+"F1.wireOp",EDGE,"E17.bottom");var subQ4=makeQuery(id+"F1.imprint","INTERSECT",VERTEX,{"derivedFrom":[subQ3,subQ0]});Q12=makeQuery(id+"F1.imprint","IMPRINT",FACE,{"disambiguationData":[TD([[makeQuery(id+"F1.imprint","IMPRINT",EDGE,{"disambiguationData":[TD([[subQ4,1.0]])],"derivedFrom":subQ3}),-1.0]])]});}
            var Q13;
            {var subQ5=sQuery(id+"F1.wireOp",EDGE,"E25.4.0.0");Q13=makeQuery(id+"F1.imprint","IMPRINT",FACE,{"disambiguationData":[TD([[makeQuery(id+"F1.imprint","IMPRINT",EDGE,{"derivedFrom":subQ5}),1.0]])]});}
            var Q14;
            {var subQ5=sQuery(id+"F1.wireOp",EDGE,"E25.4.0.1");Q14=makeQuery(id+"F1.imprint","IMPRINT",FACE,{"disambiguationData":[TD([[makeQuery(id+"F1.imprint","IMPRINT",EDGE,{"derivedFrom":subQ5}),-1.0]])]});}
            var Q15;
            {var subQ0=sQuery(id+"F1.wireOp",EDGE,"E19.5.0.0");var subQ3=sQuery(id+"F1.wireOp",EDGE,"E17.bottom");var subQ4=makeQuery(id+"F1.imprint","INTERSECT",VERTEX,{"derivedFrom":[subQ3,subQ0]});Q15=makeQuery(id+"F1.imprint","IMPRINT",FACE,{"disambiguationData":[TD([[makeQuery(id+"F1.imprint","IMPRINT",EDGE,{"disambiguationData":[TD([[subQ4,1.0]])],"derivedFrom":subQ3}),-1.0]])]});}
            var Q16;
            {var subQ5=sQuery(id+"F1.wireOp",EDGE,"E25.5.0.0");Q16=makeQuery(id+"F1.imprint","IMPRINT",FACE,{"disambiguationData":[TD([[makeQuery(id+"F1.imprint","IMPRINT",EDGE,{"derivedFrom":subQ5}),1.0]])]});}
            var Q17;
            {var subQ5=sQuery(id+"F1.wireOp",EDGE,"o7LFFfXf-XPDj-YDJ7-bAYC-L3mfDlW3X8TR.bottom");Q17=makeQuery(id+"F1.imprint","IMPRINT",FACE,{"disambiguationData":[TD([[makeQuery(id+"F1.imprint","IMPRINT",EDGE,{"derivedFrom":subQ5}),1.0]])]});}
            var Q18;
            {var subQ5=sQuery(id+"F1.wireOp",EDGE,"E25.6.0.0");Q18=makeQuery(id+"F1.imprint","IMPRINT",FACE,{"disambiguationData":[TD([[makeQuery(id+"F1.imprint","IMPRINT",EDGE,{"derivedFrom":subQ5}),1.0]])]});}
            var Q19;
            Q19=makeQuery(id+"F1.imprint","IMPRINT",FACE,{"disambiguationData":[TD([[makeQuery(id+"F1.imprint","IMPRINT",EDGE,{"derivedFrom":sQuery(id+"F1.wireOp",EDGE,"E19.7.0.0")}),-1.0]])]});
            var Q20;
            {var subQ5=sQuery(id+"F1.wireOp",EDGE,"E25.6.0.1");Q20=makeQuery(id+"F1.imprint","IMPRINT",FACE,{"disambiguationData":[TD([[makeQuery(id+"F1.imprint","IMPRINT",EDGE,{"derivedFrom":subQ5}),-1.0]])]});}
            var Q21;
            {var subQ5=sQuery(id+"F1.wireOp",EDGE,"E25.5.0.1");Q21=makeQuery(id+"F1.imprint","IMPRINT",FACE,{"disambiguationData":[TD([[makeQuery(id+"F1.imprint","IMPRINT",EDGE,{"derivedFrom":subQ5}),-1.0]])]});}
            var Q22;
            {var subQ6=sQuery(id+"F1.wireOp",EDGE,"E92.top");Q22=makeQuery(id+"F1.imprint","IMPRINT",FACE,{"disambiguationData":[TD([[makeQuery(id+"F1.imprint","IMPRINT",EDGE,{"derivedFrom":subQ6}),-1.0]])]});}
            var Q23;
            {var subQ3=sQuery(id+"F1.wireOp",EDGE,"E107.bottom");Q23=makeQuery(id+"F1.imprint","IMPRINT",FACE,{"disambiguationData":[TD([[makeQuery(id+"F1.imprint","IMPRINT",EDGE,{"derivedFrom":subQ3}),-1.0]])]});}
            var Q24;
            Q24=makeQuery(id+"F1.imprint","IMPRINT",FACE,{"disambiguationData":[TD([[makeQuery(id+"F1.imprint","IMPRINT",EDGE,{"derivedFrom":sQuery(id+"F1.wireOp",EDGE,"E108.bottom")}),-1.0]])]});
            var Q25;
            {var subQ2=sQuery(id+"F1.wireOp",EDGE,"OE6oFQgg-1iZH-lJda-pF8F-zLQ9cKPHJxX8");Q25=makeQuery(id+"F1.imprint","IMPRINT",FACE,{"disambiguationData":[TD([[makeQuery(id+"F1.imprint","IMPRINT",EDGE,{"derivedFrom":subQ2}),1.0]])]});}
            var Q26;
            Q26=makeQuery(id+"F1.imprint","IMPRINT",FACE,{"disambiguationData":[TD([[makeQuery(id+"F1.imprint","IMPRINT",EDGE,{"derivedFrom":sQuery(id+"F1.wireOp",EDGE,"E109.bottom")}),1.0]])]});
            var Q27;
            {var subQ0=sQuery(id+"F1.wireOp",EDGE,"E19.6.0.0");var subQ5=sQuery(id+"F1.wireOp",EDGE,"E17.bottom");var subQ6=makeQuery(id+"F1.imprint","INTERSECT",VERTEX,{"derivedFrom":[subQ5,subQ0]});Q27=makeQuery(id+"F1.imprint","IMPRINT",FACE,{"disambiguationData":[TD([[makeQuery(id+"F1.imprint","IMPRINT",EDGE,{"disambiguationData":[TD([[subQ6,1.0]])],"derivedFrom":subQ5}),-1.0]])]});}
            var Q28;
            {var subQ3=sQuery(id+"F1.wireOp",EDGE,"E20");Q28=makeQuery(id+"F1.imprint","IMPRINT",FACE,{"disambiguationData":[TD([[makeQuery(id+"F1.imprint","IMPRINT",EDGE,{"derivedFrom":subQ3}),1.0]])]});}
            var Q29;
            {var subQ1=sQuery(id+"F1.wireOp",EDGE,"E116.left");Q29=makeQuery(id+"F1.imprint","IMPRINT",FACE,{"disambiguationData":[TD([[makeQuery(id+"F1.imprint","IMPRINT",EDGE,{"derivedFrom":subQ1}),1.0]])]});}
            var Q30;
            {var subQ5=sQuery(id+"F1.wireOp",EDGE,"E124");Q30=makeQuery(id+"F1.imprint","IMPRINT",FACE,{"disambiguationData":[TD([[makeQuery(id+"F1.imprint","IMPRINT",EDGE,{"derivedFrom":subQ5}),-1.0]])]});}
            extrude(context, id + "F4", {"entities" : qUnion([Q0, Q1, Q2, Q3, Q4, Q5, Q6, Q7, Q8, Q9, Q10, Q11, Q12, Q13, Q14, Q15, Q16, Q17, Q18, Q19, Q20, Q21, Q22, Q23, Q24, Q25, Q26, Q27, Q28, Q29, Q30]), "depth" : 18.03 * mm});
        }
        {
            var Q0;
            Q0=makeQuery(id+"F4.opExtrude","SWEPT_EDGE",EDGE,{"disambiguationData":[OSD([sQuery(id+"F1.wireOp",EDGE,"E93"),sQuery(id+"F1.wireOp",EDGE,"E120")])]});
            var Q1;
            Q1=makeQuery(id+"F4.opExtrude","SWEPT_EDGE",EDGE,{"disambiguationData":[OSD([sQuery(id+"F1.wireOp",EDGE,"E92.left"),sQuery(id+"F1.wireOp",EDGE,"E93")])]});
            var Q2;
            Q2=makeQuery(id+"F4.opExtrude","SWEPT_EDGE",EDGE,{"disambiguationData":[OSD([sQuery(id+"F1.wireOp",EDGE,"E92.right"),sQuery(id+"F1.wireOp",EDGE,"E122")])]});
            var Q3;
            Q3=makeQuery(id+"F4.opExtrude","SWEPT_EDGE",EDGE,{"disambiguationData":[OSD([sQuery(id+"F1.wireOp",EDGE,"E120"),sQuery(id+"F1.wireOp",EDGE,"E122")])]});
            fillet(context, id + "F5", {"entities" : qUnion([Q0, Q1, Q2, Q3]), "radius" : 127 * mm, "tangentPropagation" : true, "allowEdgeOverflow" : false});
        }
        {
            var Q0;
            Q0=makeQuery(id+"F4.opExtrude","SWEPT_EDGE",EDGE,{"disambiguationData":[OSD([sQuery(id+"F1.wireOp",EDGE,"E107.bottom"),sQuery(id+"F1.wireOp",EDGE,"E107.right")])]});
            fillet(context, id + "F6", {"entities" : qUnion([Q0]), "radius" : 12.7 * mm, "tangentPropagation" : true, "allowEdgeOverflow" : false});
        }
    });
